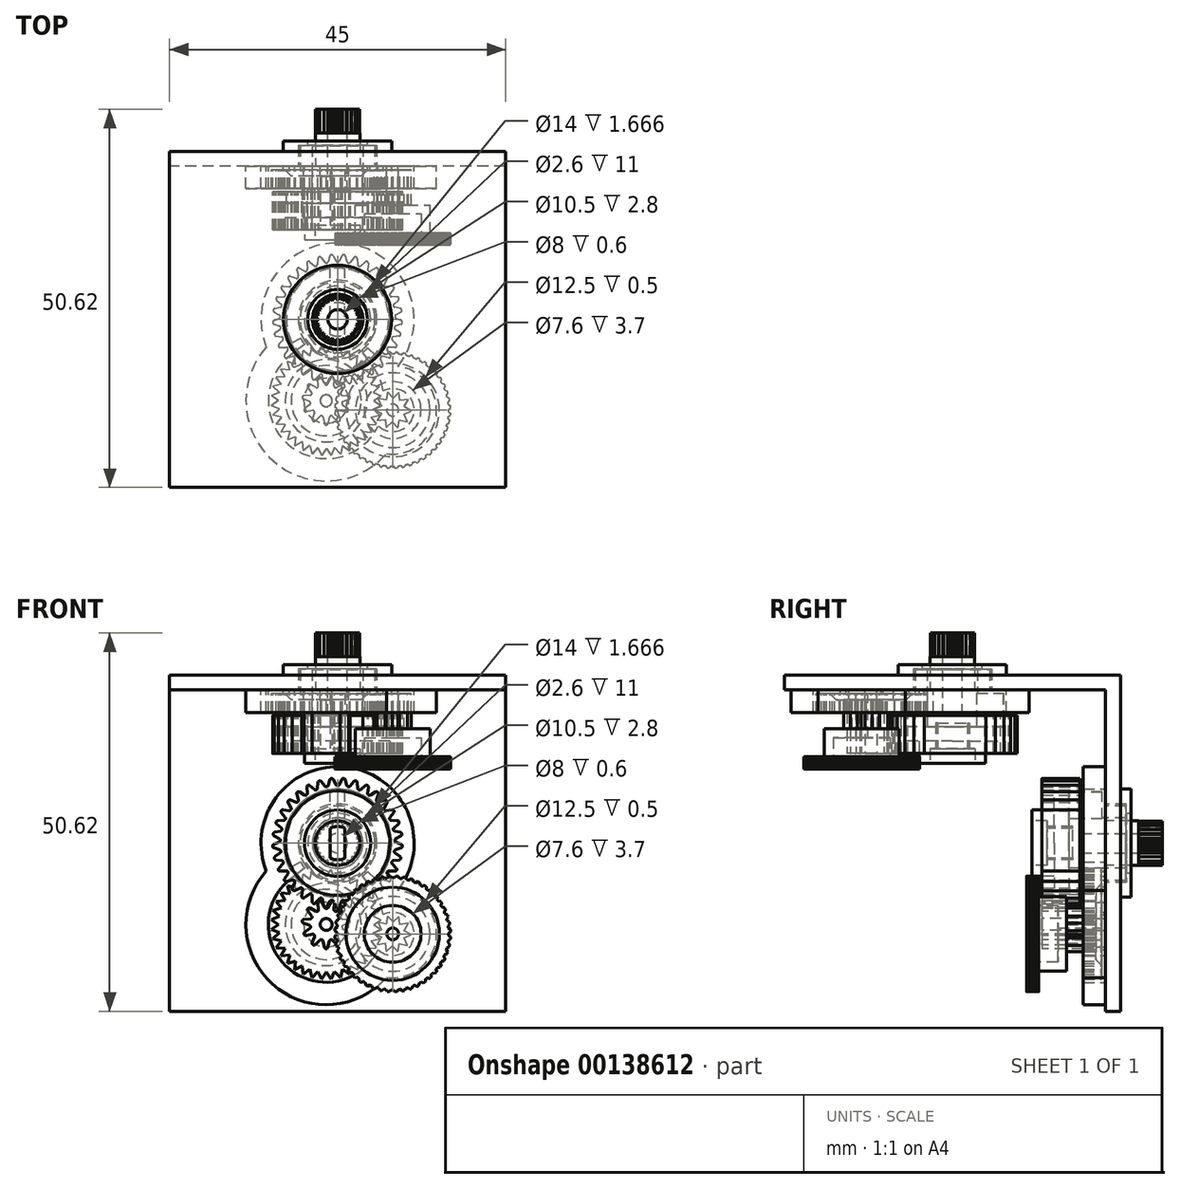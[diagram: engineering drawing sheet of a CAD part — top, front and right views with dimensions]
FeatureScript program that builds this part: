
annotation { "Feature Type Name" : "Feature", "Feature Type Description" : "" }
export const myFeature = defineFeature(function(context is Context, id is Id, definition is map)
    precondition{}
    {
        {
            var Q0;
            Q0=qCreatedBy(makeId("Front.planeOp"),FACE);
            var sketch = newSketch(context, id + "F0", { "sketchPlane" : qUnion([Q0])});
            skLineSegment(sketch, "E0", {"start": v(0, 0) * mm, "end": v(0, 17.46) * mm, "construction": true});
            skLineSegment(sketch, "E1", {"start": v(0, 0) * mm, "end": v(-4.45, 0) * mm});
            skLineSegment(sketch, "E2", {"start": v(-4.45, 0) * mm, "end": v(-4.45, 1.33) * mm});
            skLineSegment(sketch, "E3", {"start": v(-4.45, 1.33) * mm, "end": v(-8.7, 1.33) * mm});
            skLineSegment(sketch, "E4", {"start": v(-8.7, 1.33) * mm, "end": v(-8.7, 6.41) * mm});
            skLineSegment(sketch, "E5", {"start": v(-8.7, 6.41) * mm, "end": v(-3.38, 6.41) * mm});
            skLineSegment(sketch, "E6", {"start": v(-3.38, 6.41) * mm, "end": v(-3.38, 9.84) * mm});
            skLineSegment(sketch, "E7", {"start": v(-3.38, 9.84) * mm, "end": v(-2.98, 9.84) * mm});
            skLineSegment(sketch, "E8", {"start": v(-2.98, 9.84) * mm, "end": v(-2.98, 13.97) * mm});
            skLineSegment(sketch, "E9", {"start": v(-2.98, 13.97) * mm, "end": v(-2.98, 17.46) * mm});
            skLineSegment(sketch, "E10", {"start": v(-2.98, 17.46) * mm, "end": v(0, 17.46) * mm});
            skLineSegment(sketch, "E11", {"start": v(0, 0) * mm, "end": v(0, 17.46) * mm});
            skSolve(sketch);
        }
        {
            var Q0;
            Q0 = qSketchRegion(id + "F0", true);
            var Q1;
            Q1=sQuery(id+"F0.wireOp",EDGE,"E0");
            revolve(context, id + "F1", {"entities" : qUnion([Q0]), "axis" : qUnion([Q1]), "revolveType" : RevolveType.FULL});
        }
        {
            var Q0;
            Q0=makeQuery(id+"F1.opRevolve","SWEPT_FACE",FACE,{"disambiguationData":[OSD([sQuery(id+"F0.wireOp",EDGE,"E10")])]});
            var sketch = newSketch(context, id + "F2", { "sketchPlane" : qUnion([Q0])});
            skLineSegment(sketch, "E12", {"start": v(0, 0) * mm, "end": v(0, 2.98) * mm, "construction": true});
            skLineSegment(sketch, "E13", {"start": v(0, 0) * mm, "end": v(-0.39, 2.96) * mm, "construction": true});
            skLineSegment(sketch, "E14.MirrorCS", {"start": v(0, 0) * mm, "end": v(0.39, 2.96) * mm, "construction": true});
            skLineSegment(sketch, "E15", {"start": v(-0.39, 2.96) * mm, "end": v(0, 2.6) * mm});
            skLineSegment(sketch, "E16", {"start": v(0, 2.6) * mm, "end": v(0.39, 2.96) * mm});
            skLineSegment(sketch, "E17.1.0", {"start": v(-1.14, 2.76) * mm, "end": v(-0.67, 2.51) * mm});
            skLineSegment(sketch, "E17.1.1", {"start": v(-0.67, 2.51) * mm, "end": v(-0.39, 2.96) * mm});
            skLineSegment(sketch, "E17.2.0", {"start": v(-1.82, 2.37) * mm, "end": v(-1.3, 2.25) * mm});
            skLineSegment(sketch, "E17.2.1", {"start": v(-1.3, 2.25) * mm, "end": v(-1.14, 2.76) * mm});
            skLineSegment(sketch, "E17.3.0", {"start": v(-2.37, 1.82) * mm, "end": v(-1.84, 1.84) * mm});
            skLineSegment(sketch, "E17.3.1", {"start": v(-1.84, 1.84) * mm, "end": v(-1.82, 2.37) * mm});
            skLineSegment(sketch, "E17.4.0", {"start": v(-2.76, 1.14) * mm, "end": v(-2.25, 1.3) * mm});
            skLineSegment(sketch, "E17.4.1", {"start": v(-2.25, 1.3) * mm, "end": v(-2.37, 1.82) * mm});
            skLineSegment(sketch, "E17.5.0", {"start": v(-2.96, 0.39) * mm, "end": v(-2.51, 0.67) * mm});
            skLineSegment(sketch, "E17.5.1", {"start": v(-2.51, 0.67) * mm, "end": v(-2.76, 1.14) * mm});
            skLineSegment(sketch, "E17.6.0", {"start": v(-2.96, -0.39) * mm, "end": v(-2.6, 0) * mm});
            skLineSegment(sketch, "E17.6.1", {"start": v(-2.6, 0) * mm, "end": v(-2.96, 0.39) * mm});
            skLineSegment(sketch, "E17.7.0", {"start": v(-2.76, -1.14) * mm, "end": v(-2.51, -0.67) * mm});
            skLineSegment(sketch, "E17.7.1", {"start": v(-2.51, -0.67) * mm, "end": v(-2.96, -0.39) * mm});
            skLineSegment(sketch, "E17.8.0", {"start": v(-2.37, -1.82) * mm, "end": v(-2.25, -1.3) * mm});
            skLineSegment(sketch, "E17.8.1", {"start": v(-2.25, -1.3) * mm, "end": v(-2.76, -1.14) * mm});
            skLineSegment(sketch, "E17.9.0", {"start": v(-1.82, -2.37) * mm, "end": v(-1.84, -1.84) * mm});
            skLineSegment(sketch, "E17.9.1", {"start": v(-1.84, -1.84) * mm, "end": v(-2.37, -1.82) * mm});
            skLineSegment(sketch, "E17.10.0", {"start": v(-1.14, -2.76) * mm, "end": v(-1.3, -2.25) * mm});
            skLineSegment(sketch, "E17.10.1", {"start": v(-1.3, -2.25) * mm, "end": v(-1.82, -2.37) * mm});
            skLineSegment(sketch, "E17.11.0", {"start": v(-0.39, -2.96) * mm, "end": v(-0.67, -2.51) * mm});
            skLineSegment(sketch, "E17.11.1", {"start": v(-0.67, -2.51) * mm, "end": v(-1.14, -2.76) * mm});
            skLineSegment(sketch, "E17.12.0", {"start": v(0.39, -2.96) * mm, "end": v(0, -2.6) * mm});
            skLineSegment(sketch, "E17.12.1", {"start": v(0, -2.6) * mm, "end": v(-0.39, -2.96) * mm});
            skLineSegment(sketch, "E17.13.0", {"start": v(1.14, -2.76) * mm, "end": v(0.67, -2.51) * mm});
            skLineSegment(sketch, "E17.13.1", {"start": v(0.67, -2.51) * mm, "end": v(0.39, -2.96) * mm});
            skLineSegment(sketch, "E17.14.0", {"start": v(1.82, -2.37) * mm, "end": v(1.3, -2.25) * mm});
            skLineSegment(sketch, "E17.14.1", {"start": v(1.3, -2.25) * mm, "end": v(1.14, -2.76) * mm});
            skLineSegment(sketch, "E17.15.0", {"start": v(2.37, -1.82) * mm, "end": v(1.84, -1.84) * mm});
            skLineSegment(sketch, "E17.15.1", {"start": v(1.84, -1.84) * mm, "end": v(1.82, -2.37) * mm});
            skLineSegment(sketch, "E17.16.0", {"start": v(2.76, -1.14) * mm, "end": v(2.25, -1.3) * mm});
            skLineSegment(sketch, "E17.16.1", {"start": v(2.25, -1.3) * mm, "end": v(2.37, -1.82) * mm});
            skLineSegment(sketch, "E17.17.0", {"start": v(2.96, -0.39) * mm, "end": v(2.51, -0.67) * mm});
            skLineSegment(sketch, "E17.17.1", {"start": v(2.51, -0.67) * mm, "end": v(2.76, -1.14) * mm});
            skLineSegment(sketch, "E17.18.0", {"start": v(2.96, 0.39) * mm, "end": v(2.6, 0) * mm});
            skLineSegment(sketch, "E17.18.1", {"start": v(2.6, 0) * mm, "end": v(2.96, -0.39) * mm});
            skLineSegment(sketch, "E17.19.0", {"start": v(2.76, 1.14) * mm, "end": v(2.51, 0.67) * mm});
            skLineSegment(sketch, "E17.19.1", {"start": v(2.51, 0.67) * mm, "end": v(2.96, 0.39) * mm});
            skLineSegment(sketch, "E17.20.0", {"start": v(2.37, 1.82) * mm, "end": v(2.25, 1.3) * mm});
            skLineSegment(sketch, "E17.20.1", {"start": v(2.25, 1.3) * mm, "end": v(2.76, 1.14) * mm});
            skLineSegment(sketch, "E17.21.0", {"start": v(1.82, 2.37) * mm, "end": v(1.84, 1.84) * mm});
            skLineSegment(sketch, "E17.21.1", {"start": v(1.84, 1.84) * mm, "end": v(2.37, 1.82) * mm});
            skLineSegment(sketch, "E17.22.0", {"start": v(1.14, 2.76) * mm, "end": v(1.3, 2.25) * mm});
            skLineSegment(sketch, "E17.22.1", {"start": v(1.3, 2.25) * mm, "end": v(1.82, 2.37) * mm});
            skLineSegment(sketch, "E17.23.0", {"start": v(0.39, 2.96) * mm, "end": v(0.67, 2.51) * mm});
            skLineSegment(sketch, "E17.23.1", {"start": v(0.67, 2.51) * mm, "end": v(1.14, 2.76) * mm});
            skPoint(sketch, "E17.center", {"position": v(0, 0) * mm});
            skSolve(sketch);
        }
        {
            var Q0;
            {var subQ0=sQuery(id+"F2.wireOp",EDGE,"E17.2.0");Q0=makeQuery(id+"F2.imprint","IMPRINT",FACE,{"disambiguationData":[TD([[makeQuery(id+"F2.imprint","IMPRINT",EDGE,{"derivedFrom":subQ0}),1.0]])]});}
            var Q1;
            {var subQ0=sQuery(id+"F2.wireOp",EDGE,"E17.1.0");Q1=makeQuery(id+"F2.imprint","IMPRINT",FACE,{"disambiguationData":[TD([[makeQuery(id+"F2.imprint","IMPRINT",EDGE,{"derivedFrom":subQ0}),1.0]])]});}
            var Q2;
            {var subQ0=sQuery(id+"F2.wireOp",EDGE,"E15");Q2=makeQuery(id+"F2.imprint","IMPRINT",FACE,{"disambiguationData":[TD([[makeQuery(id+"F2.imprint","IMPRINT",EDGE,{"derivedFrom":subQ0}),1.0]])]});}
            var Q3;
            {var subQ0=sQuery(id+"F2.wireOp",EDGE,"E17.23.0");Q3=makeQuery(id+"F2.imprint","IMPRINT",FACE,{"disambiguationData":[TD([[makeQuery(id+"F2.imprint","IMPRINT",EDGE,{"derivedFrom":subQ0}),1.0]])]});}
            var Q4;
            {var subQ0=sQuery(id+"F2.wireOp",EDGE,"E17.22.0");Q4=makeQuery(id+"F2.imprint","IMPRINT",FACE,{"disambiguationData":[TD([[makeQuery(id+"F2.imprint","IMPRINT",EDGE,{"derivedFrom":subQ0}),1.0]])]});}
            var Q5;
            {var subQ0=sQuery(id+"F2.wireOp",EDGE,"E17.21.0");Q5=makeQuery(id+"F2.imprint","IMPRINT",FACE,{"disambiguationData":[TD([[makeQuery(id+"F2.imprint","IMPRINT",EDGE,{"derivedFrom":subQ0}),1.0]])]});}
            var Q6;
            {var subQ0=sQuery(id+"F2.wireOp",EDGE,"E17.20.0");Q6=makeQuery(id+"F2.imprint","IMPRINT",FACE,{"disambiguationData":[TD([[makeQuery(id+"F2.imprint","IMPRINT",EDGE,{"derivedFrom":subQ0}),1.0]])]});}
            var Q7;
            {var subQ0=sQuery(id+"F2.wireOp",EDGE,"E17.19.0");Q7=makeQuery(id+"F2.imprint","IMPRINT",FACE,{"disambiguationData":[TD([[makeQuery(id+"F2.imprint","IMPRINT",EDGE,{"derivedFrom":subQ0}),1.0]])]});}
            var Q8;
            {var subQ0=sQuery(id+"F2.wireOp",EDGE,"E17.18.0");Q8=makeQuery(id+"F2.imprint","IMPRINT",FACE,{"disambiguationData":[TD([[makeQuery(id+"F2.imprint","IMPRINT",EDGE,{"derivedFrom":subQ0}),1.0]])]});}
            var Q9;
            {var subQ0=sQuery(id+"F2.wireOp",EDGE,"E17.17.0");Q9=makeQuery(id+"F2.imprint","IMPRINT",FACE,{"disambiguationData":[TD([[makeQuery(id+"F2.imprint","IMPRINT",EDGE,{"derivedFrom":subQ0}),1.0]])]});}
            var Q10;
            {var subQ0=sQuery(id+"F2.wireOp",EDGE,"E17.16.0");Q10=makeQuery(id+"F2.imprint","IMPRINT",FACE,{"disambiguationData":[TD([[makeQuery(id+"F2.imprint","IMPRINT",EDGE,{"derivedFrom":subQ0}),1.0]])]});}
            var Q11;
            {var subQ0=sQuery(id+"F2.wireOp",EDGE,"E17.15.0");Q11=makeQuery(id+"F2.imprint","IMPRINT",FACE,{"disambiguationData":[TD([[makeQuery(id+"F2.imprint","IMPRINT",EDGE,{"derivedFrom":subQ0}),1.0]])]});}
            var Q12;
            {var subQ0=sQuery(id+"F2.wireOp",EDGE,"E17.14.0");Q12=makeQuery(id+"F2.imprint","IMPRINT",FACE,{"disambiguationData":[TD([[makeQuery(id+"F2.imprint","IMPRINT",EDGE,{"derivedFrom":subQ0}),1.0]])]});}
            var Q13;
            {var subQ0=sQuery(id+"F2.wireOp",EDGE,"E17.13.0");Q13=makeQuery(id+"F2.imprint","IMPRINT",FACE,{"disambiguationData":[TD([[makeQuery(id+"F2.imprint","IMPRINT",EDGE,{"derivedFrom":subQ0}),1.0]])]});}
            var Q14;
            {var subQ0=sQuery(id+"F2.wireOp",EDGE,"E17.12.0");Q14=makeQuery(id+"F2.imprint","IMPRINT",FACE,{"disambiguationData":[TD([[makeQuery(id+"F2.imprint","IMPRINT",EDGE,{"derivedFrom":subQ0}),1.0]])]});}
            var Q15;
            {var subQ0=sQuery(id+"F2.wireOp",EDGE,"E17.11.0");Q15=makeQuery(id+"F2.imprint","IMPRINT",FACE,{"disambiguationData":[TD([[makeQuery(id+"F2.imprint","IMPRINT",EDGE,{"derivedFrom":subQ0}),1.0]])]});}
            var Q16;
            {var subQ0=sQuery(id+"F2.wireOp",EDGE,"E17.10.0");Q16=makeQuery(id+"F2.imprint","IMPRINT",FACE,{"disambiguationData":[TD([[makeQuery(id+"F2.imprint","IMPRINT",EDGE,{"derivedFrom":subQ0}),1.0]])]});}
            var Q17;
            {var subQ0=sQuery(id+"F2.wireOp",EDGE,"E17.9.0");Q17=makeQuery(id+"F2.imprint","IMPRINT",FACE,{"disambiguationData":[TD([[makeQuery(id+"F2.imprint","IMPRINT",EDGE,{"derivedFrom":subQ0}),1.0]])]});}
            var Q18;
            {var subQ0=sQuery(id+"F2.wireOp",EDGE,"E17.8.0");Q18=makeQuery(id+"F2.imprint","IMPRINT",FACE,{"disambiguationData":[TD([[makeQuery(id+"F2.imprint","IMPRINT",EDGE,{"derivedFrom":subQ0}),1.0]])]});}
            var Q19;
            {var subQ0=sQuery(id+"F2.wireOp",EDGE,"E17.7.0");Q19=makeQuery(id+"F2.imprint","IMPRINT",FACE,{"disambiguationData":[TD([[makeQuery(id+"F2.imprint","IMPRINT",EDGE,{"derivedFrom":subQ0}),1.0]])]});}
            var Q20;
            {var subQ0=sQuery(id+"F2.wireOp",EDGE,"E17.6.0");Q20=makeQuery(id+"F2.imprint","IMPRINT",FACE,{"disambiguationData":[TD([[makeQuery(id+"F2.imprint","IMPRINT",EDGE,{"derivedFrom":subQ0}),1.0]])]});}
            var Q21;
            {var subQ0=sQuery(id+"F2.wireOp",EDGE,"E17.5.0");Q21=makeQuery(id+"F2.imprint","IMPRINT",FACE,{"disambiguationData":[TD([[makeQuery(id+"F2.imprint","IMPRINT",EDGE,{"derivedFrom":subQ0}),1.0]])]});}
            var Q22;
            {var subQ0=sQuery(id+"F2.wireOp",EDGE,"E17.4.0");Q22=makeQuery(id+"F2.imprint","IMPRINT",FACE,{"disambiguationData":[TD([[makeQuery(id+"F2.imprint","IMPRINT",EDGE,{"derivedFrom":subQ0}),1.0]])]});}
            var Q23;
            {var subQ0=sQuery(id+"F2.wireOp",EDGE,"E17.3.0");Q23=makeQuery(id+"F2.imprint","IMPRINT",FACE,{"disambiguationData":[TD([[makeQuery(id+"F2.imprint","IMPRINT",EDGE,{"derivedFrom":subQ0}),1.0]])]});}
            extrude(context, id + "F3", {"entities" : qUnion([Q0, Q1, Q2, Q3, Q4, Q5, Q6, Q7, Q8, Q9, Q10, Q11, Q12, Q13, Q14, Q15, Q16, Q17, Q18, Q19, Q20, Q21, Q22, Q23]), "operationType" : NewBodyOperationType.REMOVE, "oppositeDirection" : true, "depth" : 3.17 * mm});
        }
        {
            var Q0;
            Q0=makeQuery(id+"F1.opRevolve","SWEPT_FACE",FACE,{"disambiguationData":[OSD([sQuery(id+"F0.wireOp",EDGE,"E5")])]});
            var sketch = newSketch(context, id + "F4", { "sketchPlane" : qUnion([Q0])});
            skLineSegment(sketch, "E18", {"start": v(0, 0) * mm, "end": v(0, 8.7) * mm, "construction": true});
            skLineSegment(sketch, "E19", {"start": v(0, 0) * mm, "end": v(-0.83, 8.66) * mm, "construction": true});
            skLineSegment(sketch, "E20.MirrorCS", {"start": v(0, 0) * mm, "end": v(0.83, 8.66) * mm, "construction": true});
            skArc(sketch, "E21", {"start": v(-0.58, 8.52) * mm, "mid": v(-0.68, 8.63) * mm, "end": v(-0.83, 8.66) * mm});
            skArc(sketch, "E22", {"start": v(-0.23, 7.82) * mm, "mid": v(0, 7.68) * mm, "end": v(0.23, 7.82) * mm});
            skLineSegment(sketch, "E23", {"start": v(-0.58, 8.52) * mm, "end": v(-0.23, 7.82) * mm});
            skLineSegment(sketch, "E24.MirrorCS", {"start": v(0.58, 8.52) * mm, "end": v(0.23, 7.82) * mm});
            skArc(sketch, "E25.MirrorC", {"start": v(0.58, 8.52) * mm, "mid": v(0.68, 8.63) * mm, "end": v(0.83, 8.66) * mm});
            skCircle(sketch, "E26", {"center": v(0, 0) * mm, "radius": 8.7 * mm});
            skArc(sketch, "E27.1.0", {"start": v(-1.7, 7.64) * mm, "mid": v(-1.45, 7.54) * mm, "end": v(-1.26, 7.73) * mm});
            skLineSegment(sketch, "E27.1.1", {"start": v(-2.18, 8.26) * mm, "end": v(-1.7, 7.64) * mm});
            skLineSegment(sketch, "E27.1.2", {"start": v(-1.05, 8.48) * mm, "end": v(-1.26, 7.73) * mm});
            skArc(sketch, "E27.1.3", {"start": v(-2.18, 8.26) * mm, "mid": v(-2.3, 8.34) * mm, "end": v(-2.45, 8.35) * mm});
            skArc(sketch, "E27.1.4", {"start": v(-1.05, 8.48) * mm, "mid": v(-0.97, 8.6) * mm, "end": v(-0.83, 8.66) * mm});
            skArc(sketch, "E27.2.0", {"start": v(-3.12, 7.18) * mm, "mid": v(-2.86, 7.13) * mm, "end": v(-2.7, 7.35) * mm});
            skLineSegment(sketch, "E27.2.1", {"start": v(-3.7, 7.7) * mm, "end": v(-3.12, 7.18) * mm});
            skLineSegment(sketch, "E27.2.2", {"start": v(-2.63, 8.12) * mm, "end": v(-2.7, 7.35) * mm});
            skArc(sketch, "E27.2.3", {"start": v(-3.7, 7.7) * mm, "mid": v(-3.84, 7.76) * mm, "end": v(-3.99, 7.73) * mm});
            skArc(sketch, "E27.2.4", {"start": v(-2.63, 8.12) * mm, "mid": v(-2.58, 8.26) * mm, "end": v(-2.45, 8.35) * mm});
            skArc(sketch, "E27.3.0", {"start": v(-4.42, 6.46) * mm, "mid": v(-4.15, 6.46) * mm, "end": v(-4.04, 6.7) * mm});
            skLineSegment(sketch, "E27.3.1", {"start": v(-5.1, 6.86) * mm, "end": v(-4.42, 6.46) * mm});
            skLineSegment(sketch, "E27.3.2", {"start": v(-4.12, 7.48) * mm, "end": v(-4.04, 6.7) * mm});
            skArc(sketch, "E27.3.3", {"start": v(-5.1, 6.86) * mm, "mid": v(-5.24, 6.9) * mm, "end": v(-5.38, 6.84) * mm});
            skArc(sketch, "E27.3.4", {"start": v(-4.12, 7.48) * mm, "mid": v(-4.1, 7.63) * mm, "end": v(-3.99, 7.73) * mm});
            skArc(sketch, "E27.4.0", {"start": v(-5.56, 5.5) * mm, "mid": v(-5.3, 5.56) * mm, "end": v(-5.23, 5.82) * mm});
            skLineSegment(sketch, "E27.4.1", {"start": v(-6.3, 5.77) * mm, "end": v(-5.56, 5.5) * mm});
            skLineSegment(sketch, "E27.4.2", {"start": v(-5.46, 6.56) * mm, "end": v(-5.23, 5.82) * mm});
            skArc(sketch, "E27.4.3", {"start": v(-6.3, 5.77) * mm, "mid": v(-6.45, 5.78) * mm, "end": v(-6.57, 5.7) * mm});
            skArc(sketch, "E27.4.4", {"start": v(-5.46, 6.56) * mm, "mid": v(-5.46, 6.71) * mm, "end": v(-5.38, 6.84) * mm});
            skArc(sketch, "E27.5.0", {"start": v(-6.5, 4.35) * mm, "mid": v(-6.26, 4.46) * mm, "end": v(-6.24, 4.72) * mm});
            skLineSegment(sketch, "E27.5.1", {"start": v(-7.27, 4.47) * mm, "end": v(-6.5, 4.35) * mm});
            skLineSegment(sketch, "E27.5.2", {"start": v(-6.6, 5.41) * mm, "end": v(-6.24, 4.72) * mm});
            skArc(sketch, "E27.5.3", {"start": v(-7.27, 4.47) * mm, "mid": v(-7.42, 4.45) * mm, "end": v(-7.53, 4.35) * mm});
            skArc(sketch, "E27.5.4", {"start": v(-6.6, 5.41) * mm, "mid": v(-6.64, 5.56) * mm, "end": v(-6.57, 5.7) * mm});
            skArc(sketch, "E27.6.0", {"start": v(-7.21, 3.04) * mm, "mid": v(-6.99, 3.2) * mm, "end": v(-7.02, 3.46) * mm});
            skLineSegment(sketch, "E27.6.1", {"start": v(-7.99, 3.02) * mm, "end": v(-7.21, 3.04) * mm});
            skLineSegment(sketch, "E27.6.2", {"start": v(-7.51, 4.06) * mm, "end": v(-7.02, 3.46) * mm});
            skArc(sketch, "E27.6.3", {"start": v(-7.99, 3.02) * mm, "mid": v(-8.13, 2.97) * mm, "end": v(-8.22, 2.85) * mm});
            skArc(sketch, "E27.6.4", {"start": v(-7.51, 4.06) * mm, "mid": v(-7.57, 4.2) * mm, "end": v(-7.53, 4.35) * mm});
            skArc(sketch, "E27.7.0", {"start": v(-7.66, 1.62) * mm, "mid": v(-7.47, 1.81) * mm, "end": v(-7.55, 2.07) * mm});
            skLineSegment(sketch, "E27.7.1", {"start": v(-8.42, 1.45) * mm, "end": v(-7.66, 1.62) * mm});
            skLineSegment(sketch, "E27.7.2", {"start": v(-8.14, 2.57) * mm, "end": v(-7.55, 2.07) * mm});
            skArc(sketch, "E27.7.3", {"start": v(-8.42, 1.45) * mm, "mid": v(-8.55, 1.37) * mm, "end": v(-8.61, 1.24) * mm});
            skArc(sketch, "E27.7.4", {"start": v(-8.14, 2.57) * mm, "mid": v(-8.23, 2.7) * mm, "end": v(-8.22, 2.85) * mm});
            skArc(sketch, "E27.8.0", {"start": v(-7.83, 0.15) * mm, "mid": v(-7.67, 0.37) * mm, "end": v(-7.8, 0.6) * mm});
            skLineSegment(sketch, "E27.8.1", {"start": v(-8.54, -0.17) * mm, "end": v(-7.83, 0.15) * mm});
            skLineSegment(sketch, "E27.8.2", {"start": v(-8.48, 0.98) * mm, "end": v(-7.8, 0.6) * mm});
            skArc(sketch, "E27.8.3", {"start": v(-8.54, -0.17) * mm, "mid": v(-8.65, -0.27) * mm, "end": v(-8.69, -0.41) * mm});
            skArc(sketch, "E27.8.4", {"start": v(-8.48, 0.98) * mm, "mid": v(-8.59, 1.09) * mm, "end": v(-8.61, 1.24) * mm});
            skArc(sketch, "E27.9.0", {"start": v(-7.71, -1.34) * mm, "mid": v(-7.6, -1.1) * mm, "end": v(-7.78, -0.89) * mm});
            skLineSegment(sketch, "E27.9.1", {"start": v(-8.35, -1.78) * mm, "end": v(-7.71, -1.34) * mm});
            skLineSegment(sketch, "E27.9.2", {"start": v(-8.52, -0.64) * mm, "end": v(-7.78, -0.89) * mm});
            skArc(sketch, "E27.9.3", {"start": v(-8.35, -1.78) * mm, "mid": v(-8.44, -1.9) * mm, "end": v(-8.45, -2.05) * mm});
            skArc(sketch, "E27.9.4", {"start": v(-8.52, -0.64) * mm, "mid": v(-8.64, -0.56) * mm, "end": v(-8.69, -0.41) * mm});
            skArc(sketch, "E27.10.0", {"start": v(-7.32, -2.77) * mm, "mid": v(-7.26, -2.51) * mm, "end": v(-7.47, -2.34) * mm});
            skLineSegment(sketch, "E27.10.1", {"start": v(-7.86, -3.33) * mm, "end": v(-7.32, -2.77) * mm});
            skLineSegment(sketch, "E27.10.2", {"start": v(-8.24, -2.24) * mm, "end": v(-7.47, -2.34) * mm});
            skArc(sketch, "E27.10.3", {"start": v(-7.86, -3.33) * mm, "mid": v(-7.93, -3.46) * mm, "end": v(-7.91, -3.61) * mm});
            skArc(sketch, "E27.10.4", {"start": v(-8.24, -2.24) * mm, "mid": v(-8.38, -2.18) * mm, "end": v(-8.45, -2.05) * mm});
            skArc(sketch, "E27.11.0", {"start": v(-6.66, -4.1) * mm, "mid": v(-6.65, -3.84) * mm, "end": v(-6.89, -3.72) * mm});
            skLineSegment(sketch, "E27.11.1", {"start": v(-7.1, -4.76) * mm, "end": v(-6.66, -4.1) * mm});
            skLineSegment(sketch, "E27.11.2", {"start": v(-7.67, -3.76) * mm, "end": v(-6.89, -3.72) * mm});
            skArc(sketch, "E27.11.3", {"start": v(-7.1, -4.76) * mm, "mid": v(-7.13, -4.9) * mm, "end": v(-7.09, -5.05) * mm});
            skArc(sketch, "E27.11.4", {"start": v(-7.67, -3.76) * mm, "mid": v(-7.81, -3.73) * mm, "end": v(-7.91, -3.61) * mm});
            skArc(sketch, "E27.12.0", {"start": v(-5.76, -5.3) * mm, "mid": v(-5.8, -5.03) * mm, "end": v(-6.06, -4.95) * mm});
            skLineSegment(sketch, "E27.12.1", {"start": v(-6.06, -6.01) * mm, "end": v(-5.76, -5.3) * mm});
            skLineSegment(sketch, "E27.12.2", {"start": v(-6.82, -5.14) * mm, "end": v(-6.06, -4.95) * mm});
            skArc(sketch, "E27.12.3", {"start": v(-6.06, -6.01) * mm, "mid": v(-6.08, -6.16) * mm, "end": v(-6, -6.3) * mm});
            skArc(sketch, "E27.12.4", {"start": v(-6.82, -5.14) * mm, "mid": v(-6.97, -5.14) * mm, "end": v(-7.09, -5.05) * mm});
            skArc(sketch, "E27.13.0", {"start": v(-4.66, -6.3) * mm, "mid": v(-4.75, -6.04) * mm, "end": v(-5.02, -6) * mm});
            skLineSegment(sketch, "E27.13.1", {"start": v(-4.81, -7.05) * mm, "end": v(-4.66, -6.3) * mm});
            skLineSegment(sketch, "E27.13.2", {"start": v(-5.72, -6.34) * mm, "end": v(-5.02, -6) * mm});
            skArc(sketch, "E27.13.3", {"start": v(-4.81, -7.05) * mm, "mid": v(-4.8, -7.2) * mm, "end": v(-4.7, -7.32) * mm});
            skArc(sketch, "E27.13.4", {"start": v(-5.72, -6.34) * mm, "mid": v(-5.87, -6.36) * mm, "end": v(-6, -6.3) * mm});
            skArc(sketch, "E27.14.0", {"start": v(-3.38, -7.06) * mm, "mid": v(-3.52, -6.83) * mm, "end": v(-3.79, -6.85) * mm});
            skLineSegment(sketch, "E27.14.1", {"start": v(-3.4, -7.84) * mm, "end": v(-3.38, -7.06) * mm});
            skLineSegment(sketch, "E27.14.2", {"start": v(-4.42, -7.3) * mm, "end": v(-3.79, -6.85) * mm});
            skArc(sketch, "E27.14.3", {"start": v(-3.4, -7.84) * mm, "mid": v(-3.35, -7.98) * mm, "end": v(-3.23, -8.08) * mm});
            skArc(sketch, "E27.14.4", {"start": v(-4.42, -7.3) * mm, "mid": v(-4.56, -7.36) * mm, "end": v(-4.7, -7.32) * mm});
            skArc(sketch, "E27.15.0", {"start": v(-1.99, -7.57) * mm, "mid": v(-2.16, -7.37) * mm, "end": v(-2.42, -7.44) * mm});
            skLineSegment(sketch, "E27.15.1", {"start": v(-1.85, -8.34) * mm, "end": v(-1.99, -7.57) * mm});
            skLineSegment(sketch, "E27.15.2", {"start": v(-2.95, -8.01) * mm, "end": v(-2.42, -7.44) * mm});
            skArc(sketch, "E27.15.3", {"start": v(-1.85, -8.34) * mm, "mid": v(-1.78, -8.47) * mm, "end": v(-1.65, -8.54) * mm});
            skArc(sketch, "E27.15.4", {"start": v(-2.95, -8.01) * mm, "mid": v(-3.08, -8.09) * mm, "end": v(-3.23, -8.08) * mm});
            skArc(sketch, "E27.16.0", {"start": v(-0.52, -7.81) * mm, "mid": v(-0.73, -7.65) * mm, "end": v(-0.97, -7.77) * mm});
            skLineSegment(sketch, "E27.16.1", {"start": v(-0.24, -8.54) * mm, "end": v(-0.52, -7.81) * mm});
            skLineSegment(sketch, "E27.16.2", {"start": v(-1.38, -8.43) * mm, "end": v(-0.97, -7.77) * mm});
            skArc(sketch, "E27.16.3", {"start": v(-0.24, -8.54) * mm, "mid": v(-0.14, -8.65) * mm, "end": v(0, -8.7) * mm});
            skArc(sketch, "E27.16.4", {"start": v(-1.38, -8.43) * mm, "mid": v(-1.5, -8.53) * mm, "end": v(-1.65, -8.54) * mm});
            skArc(sketch, "E27.17.0", {"start": v(0.97, -7.77) * mm, "mid": v(0.73, -7.65) * mm, "end": v(0.52, -7.81) * mm});
            skLineSegment(sketch, "E27.17.1", {"start": v(1.38, -8.43) * mm, "end": v(0.97, -7.77) * mm});
            skLineSegment(sketch, "E27.17.2", {"start": v(0.24, -8.54) * mm, "end": v(0.52, -7.81) * mm});
            skArc(sketch, "E27.17.3", {"start": v(1.38, -8.43) * mm, "mid": v(1.5, -8.53) * mm, "end": v(1.65, -8.54) * mm});
            skArc(sketch, "E27.17.4", {"start": v(0.24, -8.54) * mm, "mid": v(0.14, -8.65) * mm, "end": v(0, -8.7) * mm});
            skArc(sketch, "E27.18.0", {"start": v(2.42, -7.44) * mm, "mid": v(2.16, -7.37) * mm, "end": v(1.99, -7.57) * mm});
            skLineSegment(sketch, "E27.18.1", {"start": v(2.95, -8.01) * mm, "end": v(2.42, -7.44) * mm});
            skLineSegment(sketch, "E27.18.2", {"start": v(1.85, -8.34) * mm, "end": v(1.99, -7.57) * mm});
            skArc(sketch, "E27.18.3", {"start": v(2.95, -8.01) * mm, "mid": v(3.08, -8.09) * mm, "end": v(3.23, -8.08) * mm});
            skArc(sketch, "E27.18.4", {"start": v(1.85, -8.34) * mm, "mid": v(1.78, -8.47) * mm, "end": v(1.65, -8.54) * mm});
            skArc(sketch, "E27.19.0", {"start": v(3.79, -6.85) * mm, "mid": v(3.52, -6.83) * mm, "end": v(3.38, -7.06) * mm});
            skLineSegment(sketch, "E27.19.1", {"start": v(4.42, -7.3) * mm, "end": v(3.79, -6.85) * mm});
            skLineSegment(sketch, "E27.19.2", {"start": v(3.4, -7.84) * mm, "end": v(3.38, -7.06) * mm});
            skArc(sketch, "E27.19.3", {"start": v(4.42, -7.3) * mm, "mid": v(4.56, -7.36) * mm, "end": v(4.7, -7.32) * mm});
            skArc(sketch, "E27.19.4", {"start": v(3.4, -7.84) * mm, "mid": v(3.35, -7.98) * mm, "end": v(3.23, -8.08) * mm});
            skArc(sketch, "E27.20.0", {"start": v(5.02, -6) * mm, "mid": v(4.75, -6.04) * mm, "end": v(4.66, -6.3) * mm});
            skLineSegment(sketch, "E27.20.1", {"start": v(5.72, -6.34) * mm, "end": v(5.02, -6) * mm});
            skLineSegment(sketch, "E27.20.2", {"start": v(4.81, -7.05) * mm, "end": v(4.66, -6.3) * mm});
            skArc(sketch, "E27.20.3", {"start": v(5.72, -6.34) * mm, "mid": v(5.87, -6.36) * mm, "end": v(6, -6.3) * mm});
            skArc(sketch, "E27.20.4", {"start": v(4.81, -7.05) * mm, "mid": v(4.8, -7.2) * mm, "end": v(4.7, -7.32) * mm});
            skArc(sketch, "E27.21.0", {"start": v(6.06, -4.95) * mm, "mid": v(5.8, -5.03) * mm, "end": v(5.76, -5.3) * mm});
            skLineSegment(sketch, "E27.21.1", {"start": v(6.82, -5.14) * mm, "end": v(6.06, -4.95) * mm});
            skLineSegment(sketch, "E27.21.2", {"start": v(6.06, -6.01) * mm, "end": v(5.76, -5.3) * mm});
            skArc(sketch, "E27.21.3", {"start": v(6.82, -5.14) * mm, "mid": v(6.97, -5.14) * mm, "end": v(7.09, -5.05) * mm});
            skArc(sketch, "E27.21.4", {"start": v(6.06, -6.01) * mm, "mid": v(6.08, -6.16) * mm, "end": v(6, -6.3) * mm});
            skArc(sketch, "E27.22.0", {"start": v(6.89, -3.72) * mm, "mid": v(6.65, -3.84) * mm, "end": v(6.66, -4.1) * mm});
            skLineSegment(sketch, "E27.22.1", {"start": v(7.67, -3.76) * mm, "end": v(6.89, -3.72) * mm});
            skLineSegment(sketch, "E27.22.2", {"start": v(7.1, -4.76) * mm, "end": v(6.66, -4.1) * mm});
            skArc(sketch, "E27.22.3", {"start": v(7.67, -3.76) * mm, "mid": v(7.81, -3.73) * mm, "end": v(7.91, -3.61) * mm});
            skArc(sketch, "E27.22.4", {"start": v(7.1, -4.76) * mm, "mid": v(7.13, -4.9) * mm, "end": v(7.09, -5.05) * mm});
            skArc(sketch, "E27.23.0", {"start": v(7.47, -2.34) * mm, "mid": v(7.26, -2.51) * mm, "end": v(7.32, -2.77) * mm});
            skLineSegment(sketch, "E27.23.1", {"start": v(8.24, -2.24) * mm, "end": v(7.47, -2.34) * mm});
            skLineSegment(sketch, "E27.23.2", {"start": v(7.86, -3.33) * mm, "end": v(7.32, -2.77) * mm});
            skArc(sketch, "E27.23.3", {"start": v(8.24, -2.24) * mm, "mid": v(8.38, -2.18) * mm, "end": v(8.45, -2.05) * mm});
            skArc(sketch, "E27.23.4", {"start": v(7.86, -3.33) * mm, "mid": v(7.93, -3.46) * mm, "end": v(7.91, -3.61) * mm});
            skArc(sketch, "E27.24.0", {"start": v(7.78, -0.89) * mm, "mid": v(7.6, -1.1) * mm, "end": v(7.71, -1.34) * mm});
            skLineSegment(sketch, "E27.24.1", {"start": v(8.52, -0.64) * mm, "end": v(7.78, -0.89) * mm});
            skLineSegment(sketch, "E27.24.2", {"start": v(8.35, -1.78) * mm, "end": v(7.71, -1.34) * mm});
            skArc(sketch, "E27.24.3", {"start": v(8.52, -0.64) * mm, "mid": v(8.64, -0.56) * mm, "end": v(8.69, -0.41) * mm});
            skArc(sketch, "E27.24.4", {"start": v(8.35, -1.78) * mm, "mid": v(8.44, -1.9) * mm, "end": v(8.45, -2.05) * mm});
            skArc(sketch, "E27.25.0", {"start": v(7.8, 0.6) * mm, "mid": v(7.67, 0.37) * mm, "end": v(7.83, 0.15) * mm});
            skLineSegment(sketch, "E27.25.1", {"start": v(8.48, 0.98) * mm, "end": v(7.8, 0.6) * mm});
            skLineSegment(sketch, "E27.25.2", {"start": v(8.54, -0.17) * mm, "end": v(7.83, 0.15) * mm});
            skArc(sketch, "E27.25.3", {"start": v(8.48, 0.98) * mm, "mid": v(8.59, 1.09) * mm, "end": v(8.61, 1.24) * mm});
            skArc(sketch, "E27.25.4", {"start": v(8.54, -0.17) * mm, "mid": v(8.65, -0.27) * mm, "end": v(8.69, -0.41) * mm});
            skArc(sketch, "E27.26.0", {"start": v(7.55, 2.07) * mm, "mid": v(7.47, 1.81) * mm, "end": v(7.66, 1.62) * mm});
            skLineSegment(sketch, "E27.26.1", {"start": v(8.14, 2.57) * mm, "end": v(7.55, 2.07) * mm});
            skLineSegment(sketch, "E27.26.2", {"start": v(8.42, 1.45) * mm, "end": v(7.66, 1.62) * mm});
            skArc(sketch, "E27.26.3", {"start": v(8.14, 2.57) * mm, "mid": v(8.23, 2.7) * mm, "end": v(8.22, 2.85) * mm});
            skArc(sketch, "E27.26.4", {"start": v(8.42, 1.45) * mm, "mid": v(8.55, 1.37) * mm, "end": v(8.61, 1.24) * mm});
            skArc(sketch, "E27.27.0", {"start": v(7.02, 3.46) * mm, "mid": v(6.99, 3.2) * mm, "end": v(7.21, 3.04) * mm});
            skLineSegment(sketch, "E27.27.1", {"start": v(7.51, 4.06) * mm, "end": v(7.02, 3.46) * mm});
            skLineSegment(sketch, "E27.27.2", {"start": v(7.99, 3.02) * mm, "end": v(7.21, 3.04) * mm});
            skArc(sketch, "E27.27.3", {"start": v(7.51, 4.06) * mm, "mid": v(7.57, 4.2) * mm, "end": v(7.53, 4.35) * mm});
            skArc(sketch, "E27.27.4", {"start": v(7.99, 3.02) * mm, "mid": v(8.13, 2.97) * mm, "end": v(8.22, 2.85) * mm});
            skArc(sketch, "E27.28.0", {"start": v(6.24, 4.72) * mm, "mid": v(6.26, 4.46) * mm, "end": v(6.5, 4.35) * mm});
            skLineSegment(sketch, "E27.28.1", {"start": v(6.6, 5.41) * mm, "end": v(6.24, 4.72) * mm});
            skLineSegment(sketch, "E27.28.2", {"start": v(7.27, 4.47) * mm, "end": v(6.5, 4.35) * mm});
            skArc(sketch, "E27.28.3", {"start": v(6.6, 5.41) * mm, "mid": v(6.64, 5.56) * mm, "end": v(6.57, 5.7) * mm});
            skArc(sketch, "E27.28.4", {"start": v(7.27, 4.47) * mm, "mid": v(7.42, 4.45) * mm, "end": v(7.53, 4.35) * mm});
            skArc(sketch, "E27.29.0", {"start": v(5.23, 5.82) * mm, "mid": v(5.3, 5.56) * mm, "end": v(5.56, 5.5) * mm});
            skLineSegment(sketch, "E27.29.1", {"start": v(5.46, 6.56) * mm, "end": v(5.23, 5.82) * mm});
            skLineSegment(sketch, "E27.29.2", {"start": v(6.3, 5.77) * mm, "end": v(5.56, 5.5) * mm});
            skArc(sketch, "E27.29.3", {"start": v(5.46, 6.56) * mm, "mid": v(5.46, 6.71) * mm, "end": v(5.38, 6.84) * mm});
            skArc(sketch, "E27.29.4", {"start": v(6.3, 5.77) * mm, "mid": v(6.45, 5.78) * mm, "end": v(6.57, 5.7) * mm});
            skArc(sketch, "E27.30.0", {"start": v(4.04, 6.7) * mm, "mid": v(4.15, 6.46) * mm, "end": v(4.42, 6.46) * mm});
            skLineSegment(sketch, "E27.30.1", {"start": v(4.12, 7.48) * mm, "end": v(4.04, 6.7) * mm});
            skLineSegment(sketch, "E27.30.2", {"start": v(5.1, 6.86) * mm, "end": v(4.42, 6.46) * mm});
            skArc(sketch, "E27.30.3", {"start": v(4.12, 7.48) * mm, "mid": v(4.1, 7.63) * mm, "end": v(3.99, 7.73) * mm});
            skArc(sketch, "E27.30.4", {"start": v(5.1, 6.86) * mm, "mid": v(5.24, 6.9) * mm, "end": v(5.38, 6.84) * mm});
            skArc(sketch, "E27.31.0", {"start": v(2.7, 7.35) * mm, "mid": v(2.86, 7.13) * mm, "end": v(3.12, 7.18) * mm});
            skLineSegment(sketch, "E27.31.1", {"start": v(2.63, 8.12) * mm, "end": v(2.7, 7.35) * mm});
            skLineSegment(sketch, "E27.31.2", {"start": v(3.7, 7.7) * mm, "end": v(3.12, 7.18) * mm});
            skArc(sketch, "E27.31.3", {"start": v(2.63, 8.12) * mm, "mid": v(2.58, 8.26) * mm, "end": v(2.45, 8.35) * mm});
            skArc(sketch, "E27.31.4", {"start": v(3.7, 7.7) * mm, "mid": v(3.84, 7.76) * mm, "end": v(3.99, 7.73) * mm});
            skArc(sketch, "E27.32.0", {"start": v(1.26, 7.73) * mm, "mid": v(1.45, 7.54) * mm, "end": v(1.7, 7.64) * mm});
            skLineSegment(sketch, "E27.32.1", {"start": v(1.05, 8.48) * mm, "end": v(1.26, 7.73) * mm});
            skLineSegment(sketch, "E27.32.2", {"start": v(2.18, 8.26) * mm, "end": v(1.7, 7.64) * mm});
            skArc(sketch, "E27.32.3", {"start": v(1.05, 8.48) * mm, "mid": v(0.97, 8.6) * mm, "end": v(0.83, 8.66) * mm});
            skArc(sketch, "E27.32.4", {"start": v(2.18, 8.26) * mm, "mid": v(2.3, 8.34) * mm, "end": v(2.45, 8.35) * mm});
            skSolve(sketch);
        }
        {
            var Q0;
            Q0=makeQuery(id+"F4.imprint","IMPRINT",FACE,{"disambiguationData":[TD([[makeQuery(id+"F4.imprint","IMPRINT",EDGE,{"derivedFrom":sQuery(id+"F4.wireOp",EDGE,"E27.3.0")}),1.0]])]});
            var Q1;
            Q1=makeQuery(id+"F4.imprint","IMPRINT",FACE,{"disambiguationData":[TD([[makeQuery(id+"F4.imprint","IMPRINT",EDGE,{"derivedFrom":sQuery(id+"F4.wireOp",EDGE,"E27.2.0")}),1.0]])]});
            var Q2;
            Q2=makeQuery(id+"F4.imprint","IMPRINT",FACE,{"disambiguationData":[TD([[makeQuery(id+"F4.imprint","IMPRINT",EDGE,{"derivedFrom":sQuery(id+"F4.wireOp",EDGE,"E27.1.0")}),1.0]])]});
            var Q3;
            {var subQ1=sQuery(id+"F4.wireOp",EDGE,"E21");Q3=makeQuery(id+"F4.imprint","IMPRINT",FACE,{"disambiguationData":[TD([[makeQuery(id+"F4.imprint","IMPRINT",EDGE,{"derivedFrom":subQ1}),-1.0]])]});}
            var Q4;
            Q4=makeQuery(id+"F4.imprint","IMPRINT",FACE,{"disambiguationData":[TD([[makeQuery(id+"F4.imprint","IMPRINT",EDGE,{"derivedFrom":sQuery(id+"F4.wireOp",EDGE,"E27.32.0")}),1.0]])]});
            var Q5;
            Q5=makeQuery(id+"F4.imprint","IMPRINT",FACE,{"disambiguationData":[TD([[makeQuery(id+"F4.imprint","IMPRINT",EDGE,{"derivedFrom":sQuery(id+"F4.wireOp",EDGE,"E27.31.0")}),1.0]])]});
            var Q6;
            Q6=makeQuery(id+"F4.imprint","IMPRINT",FACE,{"disambiguationData":[TD([[makeQuery(id+"F4.imprint","IMPRINT",EDGE,{"derivedFrom":sQuery(id+"F4.wireOp",EDGE,"E27.30.0")}),1.0]])]});
            var Q7;
            Q7=makeQuery(id+"F4.imprint","IMPRINT",FACE,{"disambiguationData":[TD([[makeQuery(id+"F4.imprint","IMPRINT",EDGE,{"derivedFrom":sQuery(id+"F4.wireOp",EDGE,"E27.29.0")}),1.0]])]});
            var Q8;
            Q8=makeQuery(id+"F4.imprint","IMPRINT",FACE,{"disambiguationData":[TD([[makeQuery(id+"F4.imprint","IMPRINT",EDGE,{"derivedFrom":sQuery(id+"F4.wireOp",EDGE,"E27.28.0")}),1.0]])]});
            var Q9;
            Q9=makeQuery(id+"F4.imprint","IMPRINT",FACE,{"disambiguationData":[TD([[makeQuery(id+"F4.imprint","IMPRINT",EDGE,{"derivedFrom":sQuery(id+"F4.wireOp",EDGE,"E27.27.0")}),1.0]])]});
            var Q10;
            Q10=makeQuery(id+"F4.imprint","IMPRINT",FACE,{"disambiguationData":[TD([[makeQuery(id+"F4.imprint","IMPRINT",EDGE,{"derivedFrom":sQuery(id+"F4.wireOp",EDGE,"E27.26.0")}),1.0]])]});
            var Q11;
            Q11=makeQuery(id+"F4.imprint","IMPRINT",FACE,{"disambiguationData":[TD([[makeQuery(id+"F4.imprint","IMPRINT",EDGE,{"derivedFrom":sQuery(id+"F4.wireOp",EDGE,"E27.25.0")}),1.0]])]});
            var Q12;
            Q12=makeQuery(id+"F4.imprint","IMPRINT",FACE,{"disambiguationData":[TD([[makeQuery(id+"F4.imprint","IMPRINT",EDGE,{"derivedFrom":sQuery(id+"F4.wireOp",EDGE,"E27.24.0")}),1.0]])]});
            var Q13;
            Q13=makeQuery(id+"F4.imprint","IMPRINT",FACE,{"disambiguationData":[TD([[makeQuery(id+"F4.imprint","IMPRINT",EDGE,{"derivedFrom":sQuery(id+"F4.wireOp",EDGE,"E27.23.0")}),1.0]])]});
            var Q14;
            Q14=makeQuery(id+"F4.imprint","IMPRINT",FACE,{"disambiguationData":[TD([[makeQuery(id+"F4.imprint","IMPRINT",EDGE,{"derivedFrom":sQuery(id+"F4.wireOp",EDGE,"E27.22.0")}),1.0]])]});
            var Q15;
            Q15=makeQuery(id+"F4.imprint","IMPRINT",FACE,{"disambiguationData":[TD([[makeQuery(id+"F4.imprint","IMPRINT",EDGE,{"derivedFrom":sQuery(id+"F4.wireOp",EDGE,"E27.21.0")}),1.0]])]});
            var Q16;
            Q16=makeQuery(id+"F4.imprint","IMPRINT",FACE,{"disambiguationData":[TD([[makeQuery(id+"F4.imprint","IMPRINT",EDGE,{"derivedFrom":sQuery(id+"F4.wireOp",EDGE,"E27.20.0")}),1.0]])]});
            var Q17;
            Q17=makeQuery(id+"F4.imprint","IMPRINT",FACE,{"disambiguationData":[TD([[makeQuery(id+"F4.imprint","IMPRINT",EDGE,{"derivedFrom":sQuery(id+"F4.wireOp",EDGE,"E27.19.0")}),1.0]])]});
            var Q18;
            Q18=makeQuery(id+"F4.imprint","IMPRINT",FACE,{"disambiguationData":[TD([[makeQuery(id+"F4.imprint","IMPRINT",EDGE,{"derivedFrom":sQuery(id+"F4.wireOp",EDGE,"E27.18.0")}),1.0]])]});
            var Q19;
            Q19=makeQuery(id+"F4.imprint","IMPRINT",FACE,{"disambiguationData":[TD([[makeQuery(id+"F4.imprint","IMPRINT",EDGE,{"derivedFrom":sQuery(id+"F4.wireOp",EDGE,"E27.17.0")}),1.0]])]});
            var Q20;
            Q20=makeQuery(id+"F4.imprint","IMPRINT",FACE,{"disambiguationData":[TD([[makeQuery(id+"F4.imprint","IMPRINT",EDGE,{"derivedFrom":sQuery(id+"F4.wireOp",EDGE,"E27.16.0")}),1.0]])]});
            var Q21;
            Q21=makeQuery(id+"F4.imprint","IMPRINT",FACE,{"disambiguationData":[TD([[makeQuery(id+"F4.imprint","IMPRINT",EDGE,{"derivedFrom":sQuery(id+"F4.wireOp",EDGE,"E27.14.0")}),1.0]])]});
            var Q22;
            Q22=makeQuery(id+"F4.imprint","IMPRINT",FACE,{"disambiguationData":[TD([[makeQuery(id+"F4.imprint","IMPRINT",EDGE,{"derivedFrom":sQuery(id+"F4.wireOp",EDGE,"E27.15.0")}),1.0]])]});
            var Q23;
            Q23=makeQuery(id+"F4.imprint","IMPRINT",FACE,{"disambiguationData":[TD([[makeQuery(id+"F4.imprint","IMPRINT",EDGE,{"derivedFrom":sQuery(id+"F4.wireOp",EDGE,"E27.13.0")}),1.0]])]});
            var Q24;
            Q24=makeQuery(id+"F4.imprint","IMPRINT",FACE,{"disambiguationData":[TD([[makeQuery(id+"F4.imprint","IMPRINT",EDGE,{"derivedFrom":sQuery(id+"F4.wireOp",EDGE,"E27.12.0")}),1.0]])]});
            var Q25;
            Q25=makeQuery(id+"F4.imprint","IMPRINT",FACE,{"disambiguationData":[TD([[makeQuery(id+"F4.imprint","IMPRINT",EDGE,{"derivedFrom":sQuery(id+"F4.wireOp",EDGE,"E27.11.0")}),1.0]])]});
            var Q26;
            Q26=makeQuery(id+"F4.imprint","IMPRINT",FACE,{"disambiguationData":[TD([[makeQuery(id+"F4.imprint","IMPRINT",EDGE,{"derivedFrom":sQuery(id+"F4.wireOp",EDGE,"E27.10.0")}),1.0]])]});
            var Q27;
            Q27=makeQuery(id+"F4.imprint","IMPRINT",FACE,{"disambiguationData":[TD([[makeQuery(id+"F4.imprint","IMPRINT",EDGE,{"derivedFrom":sQuery(id+"F4.wireOp",EDGE,"E27.9.0")}),1.0]])]});
            var Q28;
            Q28=makeQuery(id+"F4.imprint","IMPRINT",FACE,{"disambiguationData":[TD([[makeQuery(id+"F4.imprint","IMPRINT",EDGE,{"derivedFrom":sQuery(id+"F4.wireOp",EDGE,"E27.8.0")}),1.0]])]});
            var Q29;
            Q29=makeQuery(id+"F4.imprint","IMPRINT",FACE,{"disambiguationData":[TD([[makeQuery(id+"F4.imprint","IMPRINT",EDGE,{"derivedFrom":sQuery(id+"F4.wireOp",EDGE,"E27.7.0")}),1.0]])]});
            var Q30;
            Q30=makeQuery(id+"F4.imprint","IMPRINT",FACE,{"disambiguationData":[TD([[makeQuery(id+"F4.imprint","IMPRINT",EDGE,{"derivedFrom":sQuery(id+"F4.wireOp",EDGE,"E27.6.0")}),1.0]])]});
            var Q31;
            Q31=makeQuery(id+"F4.imprint","IMPRINT",FACE,{"disambiguationData":[TD([[makeQuery(id+"F4.imprint","IMPRINT",EDGE,{"derivedFrom":sQuery(id+"F4.wireOp",EDGE,"E27.5.0")}),1.0]])]});
            var Q32;
            Q32=makeQuery(id+"F4.imprint","IMPRINT",FACE,{"disambiguationData":[TD([[makeQuery(id+"F4.imprint","IMPRINT",EDGE,{"derivedFrom":sQuery(id+"F4.wireOp",EDGE,"E27.4.0")}),1.0]])]});
            extrude(context, id + "F5", {"entities" : qUnion([Q0, Q1, Q2, Q3, Q4, Q5, Q6, Q7, Q8, Q9, Q10, Q11, Q12, Q13, Q14, Q15, Q16, Q17, Q18, Q19, Q20, Q21, Q22, Q23, Q24, Q25, Q26, Q27, Q28, Q29, Q30, Q31, Q32]), "operationType" : NewBodyOperationType.REMOVE, "endBound" : BoundingType.THROUGH_ALL, "oppositeDirection" : true, "depth" : 5.08 * mm});
        }
        {
            var Q0;
            Q0=qCreatedBy(makeId("Top.planeOp"),FACE);
            var sketch = newSketch(context, id + "F6", { "sketchPlane" : qUnion([Q0])});
            skCircle(sketch, "E28", {"center": v(0, 0) * mm, "radius": 7 * mm});
            skCircle(sketch, "E29.0", {"center": v(0, 0) * mm, "radius": 4.45 * mm});
            skSolve(sketch);
        }
        {
            var Q0;
            Q0=makeQuery(id+"F6.imprint","IMPRINT",FACE,{"disambiguationData":[TD([[makeQuery(id+"F6.imprint","IMPRINT",EDGE,{"derivedFrom":sQuery(id+"F6.wireOp",EDGE,"E28")}),1.0]])]});
            extrude(context, id + "F7", {"entities" : qUnion([Q0]), "operationType" : NewBodyOperationType.REMOVE, "depth" : 3 * mm});
        }
        {
            var Q0;
            Q0=makeQuery(id+"F1.opRevolve","SWEPT_FACE",FACE,{"disambiguationData":[OSD([sQuery(id+"F0.wireOp",EDGE,"E1")])]});
            var sketch = newSketch(context, id + "F8", { "sketchPlane" : qUnion([Q0])});
            skCircle(sketch, "E30", {"center": v(0, 0) * mm, "radius": 3 * mm});
            skSolve(sketch);
        }
        {
            var Q0;
            Q0 = qSketchRegion(id + "F8", true);
            extrude(context, id + "F9", {"entities" : qUnion([Q0]), "operationType" : NewBodyOperationType.REMOVE, "oppositeDirection" : true, "depth" : 2 * mm});
        }
        {
            var Q0;
            Q0=makeQuery(id+"F1.opRevolve","SWEPT_FACE",FACE,{"disambiguationData":[OSD([sQuery(id+"F0.wireOp",EDGE,"E1")])]});
            var sketch = newSketch(context, id + "F10", { "sketchPlane" : qUnion([Q0])});
            skLineSegment(sketch, "E31.left", {"start": v(1, 2) * mm, "end": v(1, -2) * mm});
            skLineSegment(sketch, "E31.right", {"start": v(-1, 2) * mm, "end": v(-1, -2) * mm});
            skPoint(sketch, "E31.middle", {"position": v(0, 0) * mm});
            skArc(sketch, "E32", {"start": v(-1, -2) * mm, "mid": v(0, -2.24) * mm, "end": v(1, -2) * mm});
            skArc(sketch, "E33.trimOffspring", {"start": v(1, 2) * mm, "mid": v(0, 2.24) * mm, "end": v(-1, 2) * mm});
            skSolve(sketch);
        }
        {
            var Q0;
            Q0=makeQuery(id+"F10.imprint","IMPRINT",FACE,{"disambiguationData":[TD([[makeQuery(id+"F10.imprint","IMPRINT",EDGE,{"derivedFrom":sQuery(id+"F10.wireOp",EDGE,"E31.left")}),-1.0]])]});
            extrude(context, id + "F11", {"entities" : qUnion([Q0]), "operationType" : NewBodyOperationType.REMOVE, "oppositeDirection" : true, "depth" : 5.45 * mm});
        }
        {
            var Q0;
            Q0=makeQuery(id+"F1.opRevolve","SWEPT_FACE",FACE,{"disambiguationData":[OSD([sQuery(id+"F0.wireOp",EDGE,"E5")])]});
            var sketch = newSketch(context, id + "F12", { "sketchPlane" : qUnion([Q0])});
            skCircle(sketch, "E34", {"center": v(0, 0) * mm, "radius": 6.86 * mm});
            skCircle(sketch, "E35.0", {"center": v(0, 0) * mm, "radius": 3.38 * mm});
            skSolve(sketch);
        }
        {
            var Q0;
            Q0=makeQuery(id+"F12.imprint","IMPRINT",FACE,{"disambiguationData":[TD([[makeQuery(id+"F12.imprint","IMPRINT",EDGE,{"derivedFrom":sQuery(id+"F12.wireOp",EDGE,"E34")}),1.0]])]});
            extrude(context, id + "F13", {"entities" : qUnion([Q0]), "operationType" : NewBodyOperationType.REMOVE, "oppositeDirection" : true, "depth" : 1.5 * mm});
        }
        {
            var Q0;
            Q0=makeQuery(id+"F13.boolean.opBoolean","COPY",FACE,{"derivedFrom":makeQuery(id+"F13.opExtrude","CAP_FACE",FACE,{"disambiguationData":[OSD([sQuery(id+"F12.wireOp",EDGE,"E34"),sQuery(id+"F12.wireOp",EDGE,"E35.0")])],"isStart":false})});
            var sketch = newSketch(context, id + "F14", { "sketchPlane" : qUnion([Q0])});
            skLineSegment(sketch, "E36.left", {"start": v(-1, 3.23) * mm, "end": v(-1, 6.79) * mm});
            skLineSegment(sketch, "E36.right", {"start": v(1, 3.23) * mm, "end": v(1, 6.79) * mm});
            skArc(sketch, "E37.0", {"start": v(1, 6.79) * mm, "mid": v(0, 6.86) * mm, "end": v(-1, 6.79) * mm});
            skLineSegment(sketch, "E38", {"start": v(-1, 3.23) * mm, "end": v(1, 3.23) * mm});
            skSolve(sketch);
        }
        {
            var Q0;
            {var subQ0=sQuery(id+"F14.wireOp",EDGE,"E36.left");Q0=makeQuery(id+"F14.imprint","IMPRINT",FACE,{"disambiguationData":[TD([[makeQuery(id+"F14.imprint","IMPRINT",EDGE,{"derivedFrom":subQ0}),-1.0]])]});}
            extrude(context, id + "F15", {"entities" : qUnion([Q0]), "operationType" : NewBodyOperationType.ADD, "depth" : 4.5 * mm});
        }
        {
            var Q0;
            Q0=makeQuery(id+"F1.opRevolve","SWEPT_FACE",FACE,{"disambiguationData":[OSD([sQuery(id+"F0.wireOp",EDGE,"E7")])]});
            var sketch = newSketch(context, id + "F16", { "sketchPlane" : qUnion([Q0])});
            skCircle(sketch, "E39", {"center": v(0, 0) * mm, "radius": 3 * mm});
            skCircle(sketch, "E40", {"center": v(0, 0) * mm, "radius": 5 * mm});
            skSolve(sketch);
        }
        {
            var Q0;
            Q0=makeQuery(id+"F16.imprint","IMPRINT",FACE,{"disambiguationData":[TD([[makeQuery(id+"F16.imprint","IMPRINT",EDGE,{"derivedFrom":sQuery(id+"F16.wireOp",EDGE,"E40")}),1.0]])]});
            extrude(context, id + "F17", {"entities" : qUnion([Q0]), "depth" : 2.75 * mm});
        }
        {
            var Q0;
            Q0=makeQuery(id+"F1.opRevolve","SWEPT_FACE",FACE,{"disambiguationData":[OSD([sQuery(id+"F0.wireOp",EDGE,"E10")])]});
            var sketch = newSketch(context, id + "F18", { "sketchPlane" : qUnion([Q0])});
            skCircle(sketch, "E41", {"center": v(0, 0) * mm, "radius": 1.3 * mm});
            skSolve(sketch);
        }
        {
            var Q0;
            Q0=makeQuery(id+"F18.imprint","IMPRINT",FACE,{"disambiguationData":[TD([[makeQuery(id+"F18.imprint","IMPRINT",EDGE,{"derivedFrom":sQuery(id+"F18.wireOp",EDGE,"E41")}),1.0]])]});
            extrude(context, id + "F19", {"entities" : qUnion([Q0]), "operationType" : NewBodyOperationType.REMOVE, "oppositeDirection" : true, "depth" : 11 * mm});
        }
        {
            var Q0;
            Q0=makeQuery(id+"F17.opExtrude","CAP_FACE",FACE,{"disambiguationData":[OSD([sQuery(id+"F0.wireOp",EDGE,"E6"),sQuery(id+"F0.wireOp",EDGE,"E7"),sQuery(id+"F16.wireOp",EDGE,"E40")])],"isStart":true});
            var sketch = newSketch(context, id + "F20", { "sketchPlane" : qUnion([Q0])});
            skLineSegment(sketch, "E42.bottom", {"start": v(-22.5, 22.5) * mm, "end": v(22.5, 22.5) * mm});
            skLineSegment(sketch, "E42.top", {"start": v(-22.5, -22.5) * mm, "end": v(22.5, -22.5) * mm});
            skLineSegment(sketch, "E42.left", {"start": v(-22.5, 22.5) * mm, "end": v(-22.5, -22.5) * mm});
            skLineSegment(sketch, "E42.right", {"start": v(22.5, 22.5) * mm, "end": v(22.5, -22.5) * mm});
            skPoint(sketch, "E42.middle", {"position": v(0, 0) * mm});
            skCircle(sketch, "E43", {"center": v(0, 0) * mm, "radius": 11 * mm, "construction": true});
            skLineSegment(sketch, "E44", {"start": v(0, 0) * mm, "end": v(-1.53, 10.9) * mm, "construction": true});
            skCircle(sketch, "E45", {"center": v(-1.53, 10.9) * mm, "radius": 9 * mm, "construction": true});
            skCircle(sketch, "E46", {"center": v(-1.53, 10.9) * mm, "radius": 3.28 * mm, "construction": true});
            skCircle(sketch, "E47", {"center": v(-1.53, 10.9) * mm, "radius": 7.3 * mm, "construction": true});
            skCircle(sketch, "E48", {"center": v(7.38, 12.15) * mm, "radius": 5 * mm, "construction": true});
            skLineSegment(sketch, "E49", {"start": v(7.38, 12.15) * mm, "end": v(-1.53, 10.9) * mm, "construction": true});
            skCircle(sketch, "E50", {"center": v(7.38, 12.15) * mm, "radius": 2.5 * mm, "construction": true});
            skCircle(sketch, "E51", {"center": v(7.38, 12.15) * mm, "radius": 7.75 * mm, "construction": true});
            skCircle(sketch, "E52.0", {"center": v(0, 0) * mm, "radius": 5.25 * mm});
            skSolve(sketch);
        }
        {
            var Q0;
            Q0=makeQuery(id+"F20.imprint","IMPRINT",FACE,{"disambiguationData":[TD([[makeQuery(id+"F20.imprint","IMPRINT",EDGE,{"derivedFrom":sQuery(id+"F20.wireOp",EDGE,"E42.bottom")}),-1.0]])]});
            extrude(context, id + "F21", {"entities" : qUnion([Q0]), "oppositeDirection" : true, "depth" : 2 * mm});
        }
        {
            var Q0;
            Q0=qCreatedBy(makeId("Front.planeOp"),FACE);
            var sketch = newSketch(context, id + "F22", { "sketchPlane" : qUnion([Q0])});
            skLineSegment(sketch, "E53", {"start": v(5.25, 11.84) * mm, "end": v(5.25, 12.64) * mm});
            skLineSegment(sketch, "E54", {"start": v(5.25, 12.64) * mm, "end": v(4, 12.64) * mm});
            skLineSegment(sketch, "E55", {"start": v(4, 12.64) * mm, "end": v(4, 13.24) * mm});
            skLineSegment(sketch, "E56", {"start": v(4, 13.24) * mm, "end": v(7.25, 13.24) * mm});
            skLineSegment(sketch, "E57", {"start": v(7.25, 13.24) * mm, "end": v(7.25, 11.84) * mm});
            skLineSegment(sketch, "E58", {"start": v(7.25, 11.84) * mm, "end": v(5.25, 11.84) * mm});
            skSolve(sketch);
        }
        {
            var Q0;
            Q0=makeQuery(id+"F22.imprint","IMPRINT",FACE,{"disambiguationData":[TD([[makeQuery(id+"F22.imprint","IMPRINT",EDGE,{"derivedFrom":sQuery(id+"F22.wireOp",EDGE,"E53")}),-1.0]])]});
            var Q1;
            Q1=makeQuery(id+"F19.boolean.opBoolean","COPY",FACE,{"derivedFrom":makeQuery(id+"F19.opExtrude","SWEPT_FACE",FACE,{"disambiguationData":[OSD([sQuery(id+"F18.wireOp",EDGE,"E41")])]})});
            revolve(context, id + "F23", {"operationType" : NewBodyOperationType.ADD, "entities" : qUnion([Q0]), "axis" : qUnion([Q1]), "revolveType" : RevolveType.FULL});
        }
        {
            var Q0;
            Q0=makeQuery(id+"F1.opRevolve","SWEPT_FACE",FACE,{"disambiguationData":[OSD([sQuery(id+"F0.wireOp",EDGE,"E3")])]});
            var sketch = newSketch(context, id + "F24", { "sketchPlane" : qUnion([Q0])});
            skPoint(sketch, "E59", {"position": v(-1.52, 10.88) * mm});
            skCircle(sketch, "E60", {"center": v(-1.52, 10.88) * mm, "radius": 3.25 * mm});
            skLineSegment(sketch, "E61", {"start": v(-1.52, 10.88) * mm, "end": v(-1.52, 14.13) * mm, "construction": true});
            skLineSegment(sketch, "E62.1.0", {"start": v(-1.52, 10.88) * mm, "end": v(-3.28, 13.62) * mm, "construction": true});
            skLineSegment(sketch, "E62.2.0", {"start": v(-1.52, 10.88) * mm, "end": v(-4.48, 12.24) * mm, "construction": true});
            skLineSegment(sketch, "E62.3.0", {"start": v(-1.52, 10.88) * mm, "end": v(-4.74, 10.42) * mm, "construction": true});
            skLineSegment(sketch, "E62.4.0", {"start": v(-1.52, 10.88) * mm, "end": v(-3.98, 8.76) * mm, "construction": true});
            skLineSegment(sketch, "E62.5.0", {"start": v(-1.52, 10.88) * mm, "end": v(-2.44, 7.77) * mm, "construction": true});
            skLineSegment(sketch, "E62.6.0", {"start": v(-1.52, 10.88) * mm, "end": v(-0.6, 7.77) * mm, "construction": true});
            skLineSegment(sketch, "E62.7.0", {"start": v(-1.52, 10.88) * mm, "end": v(0.93, 8.76) * mm, "construction": true});
            skLineSegment(sketch, "E62.8.0", {"start": v(-1.52, 10.88) * mm, "end": v(1.7, 10.42) * mm, "construction": true});
            skLineSegment(sketch, "E62.9.0", {"start": v(-1.52, 10.88) * mm, "end": v(1.43, 12.24) * mm, "construction": true});
            skLineSegment(sketch, "E62.10.0", {"start": v(-1.52, 10.88) * mm, "end": v(0.24, 13.62) * mm, "construction": true});
            skArc(sketch, "E63", {"start": v(-1.28, 13.94) * mm, "mid": v(-1.36, 14.08) * mm, "end": v(-1.52, 14.13) * mm});
            skLineSegment(sketch, "E64", {"start": v(-1.52, 10.88) * mm, "end": v(-0.6, 14) * mm, "construction": true});
            skArc(sketch, "E65", {"start": v(-1.1, 13.11) * mm, "mid": v(-0.92, 12.92) * mm, "end": v(-0.68, 12.99) * mm});
            skArc(sketch, "E66.MirrorC", {"start": v(-0.08, 13.59) * mm, "mid": v(0.07, 13.66) * mm, "end": v(0.24, 13.62) * mm});
            skLineSegment(sketch, "E67", {"start": v(-1.1, 13.11) * mm, "end": v(-1.28, 13.94) * mm});
            skLineSegment(sketch, "E68.MirrorCS", {"start": v(-0.68, 12.99) * mm, "end": v(-0.08, 13.59) * mm});
            skArc(sketch, "E69.1.0", {"start": v(-1.77, 13.94) * mm, "mid": v(-1.68, 14.08) * mm, "end": v(-1.52, 14.13) * mm});
            skLineSegment(sketch, "E69.1.1", {"start": v(-1.95, 13.11) * mm, "end": v(-1.77, 13.94) * mm});
            skArc(sketch, "E69.1.2", {"start": v(-2.37, 12.99) * mm, "mid": v(-2.12, 12.92) * mm, "end": v(-1.95, 13.11) * mm});
            skLineSegment(sketch, "E69.1.3", {"start": v(-2.37, 12.99) * mm, "end": v(-2.97, 13.59) * mm});
            skArc(sketch, "E69.1.4", {"start": v(-2.97, 13.59) * mm, "mid": v(-3.12, 13.66) * mm, "end": v(-3.28, 13.62) * mm});
            skArc(sketch, "E69.2.0", {"start": v(-3.38, 13.32) * mm, "mid": v(-3.38, 13.49) * mm, "end": v(-3.28, 13.62) * mm});
            skLineSegment(sketch, "E69.2.1", {"start": v(-3.08, 12.53) * mm, "end": v(-3.38, 13.32) * mm});
            skArc(sketch, "E69.2.2", {"start": v(-3.37, 12.2) * mm, "mid": v(-3.13, 12.28) * mm, "end": v(-3.08, 12.53) * mm});
            skLineSegment(sketch, "E69.2.3", {"start": v(-3.37, 12.2) * mm, "end": v(-4.2, 12.38) * mm});
            skArc(sketch, "E69.2.4", {"start": v(-4.2, 12.38) * mm, "mid": v(-4.36, 12.35) * mm, "end": v(-4.48, 12.24) * mm});
            skArc(sketch, "E69.3.0", {"start": v(-4.4, 11.93) * mm, "mid": v(-4.5, 12.07) * mm, "end": v(-4.48, 12.24) * mm});
            skLineSegment(sketch, "E69.3.1", {"start": v(-3.72, 11.42) * mm, "end": v(-4.4, 11.93) * mm});
            skArc(sketch, "E69.3.2", {"start": v(-3.78, 10.99) * mm, "mid": v(-3.63, 11.19) * mm, "end": v(-3.72, 11.42) * mm});
            skLineSegment(sketch, "E69.3.3", {"start": v(-3.78, 10.99) * mm, "end": v(-4.58, 10.7) * mm});
            skArc(sketch, "E69.3.4", {"start": v(-4.58, 10.7) * mm, "mid": v(-4.7, 10.59) * mm, "end": v(-4.74, 10.42) * mm});
            skArc(sketch, "E69.4.0", {"start": v(-4.5, 10.2) * mm, "mid": v(-4.66, 10.28) * mm, "end": v(-4.74, 10.42) * mm});
            skLineSegment(sketch, "E69.4.1", {"start": v(-3.66, 10.15) * mm, "end": v(-4.5, 10.2) * mm});
            skArc(sketch, "E69.4.2", {"start": v(-3.48, 9.75) * mm, "mid": v(-3.45, 10) * mm, "end": v(-3.66, 10.15) * mm});
            skLineSegment(sketch, "E69.4.3", {"start": v(-3.48, 9.75) * mm, "end": v(-3.99, 9.07) * mm});
            skArc(sketch, "E69.4.4", {"start": v(-3.99, 9.07) * mm, "mid": v(-4.04, 8.91) * mm, "end": v(-3.98, 8.76) * mm});
            skArc(sketch, "E69.5.0", {"start": v(-3.67, 8.7) * mm, "mid": v(-3.83, 8.67) * mm, "end": v(-3.98, 8.76) * mm});
            skLineSegment(sketch, "E69.5.1", {"start": v(-2.93, 9.1) * mm, "end": v(-3.67, 8.7) * mm});
            skArc(sketch, "E69.5.2", {"start": v(-2.56, 8.87) * mm, "mid": v(-2.67, 9.1) * mm, "end": v(-2.93, 9.1) * mm});
            skLineSegment(sketch, "E69.5.3", {"start": v(-2.56, 8.87) * mm, "end": v(-2.62, 8.02) * mm});
            skArc(sketch, "E69.5.4", {"start": v(-2.62, 8.02) * mm, "mid": v(-2.57, 7.86) * mm, "end": v(-2.44, 7.77) * mm});
            skArc(sketch, "E69.6.0", {"start": v(-2.15, 7.89) * mm, "mid": v(-2.27, 7.78) * mm, "end": v(-2.44, 7.77) * mm});
            skLineSegment(sketch, "E69.6.1", {"start": v(-1.74, 8.63) * mm, "end": v(-2.15, 7.89) * mm});
            skArc(sketch, "E69.6.2", {"start": v(-1.3, 8.63) * mm, "mid": v(-1.52, 8.76) * mm, "end": v(-1.74, 8.63) * mm});
            skLineSegment(sketch, "E69.6.3", {"start": v(-1.3, 8.63) * mm, "end": v(-0.9, 7.89) * mm});
            skArc(sketch, "E69.6.4", {"start": v(-0.9, 7.89) * mm, "mid": v(-0.77, 7.78) * mm, "end": v(-0.6, 7.77) * mm});
            skArc(sketch, "E69.7.0", {"start": v(-0.43, 8.02) * mm, "mid": v(-0.47, 7.86) * mm, "end": v(-0.6, 7.77) * mm});
            skLineSegment(sketch, "E69.7.1", {"start": v(-0.49, 8.87) * mm, "end": v(-0.43, 8.02) * mm});
            skArc(sketch, "E69.7.2", {"start": v(-0.12, 9.1) * mm, "mid": v(-0.37, 9.1) * mm, "end": v(-0.49, 8.87) * mm});
            skLineSegment(sketch, "E69.7.3", {"start": v(-0.12, 9.1) * mm, "end": v(0.63, 8.7) * mm});
            skArc(sketch, "E69.7.4", {"start": v(0.63, 8.7) * mm, "mid": v(0.8, 8.67) * mm, "end": v(0.93, 8.76) * mm});
            skArc(sketch, "E69.8.0", {"start": v(0.95, 9.07) * mm, "mid": v(1, 8.91) * mm, "end": v(0.93, 8.76) * mm});
            skLineSegment(sketch, "E69.8.1", {"start": v(0.44, 9.75) * mm, "end": v(0.95, 9.07) * mm});
            skArc(sketch, "E69.8.2", {"start": v(0.62, 10.15) * mm, "mid": v(0.41, 10) * mm, "end": v(0.44, 9.75) * mm});
            skLineSegment(sketch, "E69.8.3", {"start": v(0.62, 10.15) * mm, "end": v(1.47, 10.2) * mm});
            skArc(sketch, "E69.8.4", {"start": v(1.47, 10.2) * mm, "mid": v(1.62, 10.28) * mm, "end": v(1.7, 10.42) * mm});
            skArc(sketch, "E69.9.0", {"start": v(1.54, 10.7) * mm, "mid": v(1.66, 10.59) * mm, "end": v(1.7, 10.42) * mm});
            skLineSegment(sketch, "E69.9.1", {"start": v(0.74, 10.99) * mm, "end": v(1.54, 10.7) * mm});
            skArc(sketch, "E69.9.2", {"start": v(0.68, 11.42) * mm, "mid": v(0.58, 11.19) * mm, "end": v(0.74, 10.99) * mm});
            skLineSegment(sketch, "E69.9.3", {"start": v(0.68, 11.42) * mm, "end": v(1.36, 11.93) * mm});
            skArc(sketch, "E69.9.4", {"start": v(1.36, 11.93) * mm, "mid": v(1.45, 12.07) * mm, "end": v(1.43, 12.24) * mm});
            skArc(sketch, "E69.10.0", {"start": v(1.15, 12.38) * mm, "mid": v(1.32, 12.35) * mm, "end": v(1.43, 12.24) * mm});
            skLineSegment(sketch, "E69.10.1", {"start": v(0.33, 12.2) * mm, "end": v(1.15, 12.38) * mm});
            skArc(sketch, "E69.10.2", {"start": v(0.04, 12.53) * mm, "mid": v(0.08, 12.28) * mm, "end": v(0.33, 12.2) * mm});
            skLineSegment(sketch, "E69.10.3", {"start": v(0.04, 12.53) * mm, "end": v(0.33, 13.32) * mm});
            skArc(sketch, "E69.10.4", {"start": v(0.33, 13.32) * mm, "mid": v(0.34, 13.49) * mm, "end": v(0.24, 13.62) * mm});
            skCircle(sketch, "E70", {"center": v(-1.52, 10.88) * mm, "radius": 0.8 * mm});
            skSolve(sketch);
        }
        {
            var Q0;
            Q0=makeQuery(id+"F24.imprint","IMPRINT",FACE,{"disambiguationData":[TD([[makeQuery(id+"F24.imprint","IMPRINT",EDGE,{"derivedFrom":sQuery(id+"F24.wireOp",EDGE,"E63")}),1.0]])]});
            extrude(context, id + "F25", {"entities" : qUnion([Q0]), "oppositeDirection" : true, "depth" : 5.5 * mm});
        }
        {
            var Q0;
            Q0=makeQuery(id+"F25.opExtrude","CAP_FACE",FACE,{"disambiguationData":[OSD([sQuery(id+"F0.wireOp",EDGE,"E3"),sQuery(id+"F4.wireOp",EDGE,"E27.16.1"),sQuery(id+"F24.wireOp",EDGE,"E63"),sQuery(id+"F24.wireOp",EDGE,"E65"),sQuery(id+"F24.wireOp",EDGE,"E66.MirrorC"),sQuery(id+"F24.wireOp",EDGE,"E67"),sQuery(id+"F24.wireOp",EDGE,"E68.MirrorCS"),sQuery(id+"F24.wireOp",EDGE,"E69.1.0"),sQuery(id+"F24.wireOp",EDGE,"E69.1.1"),sQuery(id+"F24.wireOp",EDGE,"E69.1.2"),sQuery(id+"F24.wireOp",EDGE,"E69.1.3"),sQuery(id+"F24.wireOp",EDGE,"E69.1.4"),sQuery(id+"F24.wireOp",EDGE,"E69.2.0"),sQuery(id+"F24.wireOp",EDGE,"E69.2.1"),sQuery(id+"F24.wireOp",EDGE,"E69.2.2"),sQuery(id+"F24.wireOp",EDGE,"E69.2.3"),sQuery(id+"F24.wireOp",EDGE,"E69.2.4"),sQuery(id+"F24.wireOp",EDGE,"E69.3.0"),sQuery(id+"F24.wireOp",EDGE,"E69.3.1"),sQuery(id+"F24.wireOp",EDGE,"E69.3.2"),sQuery(id+"F24.wireOp",EDGE,"E69.3.3"),sQuery(id+"F24.wireOp",EDGE,"E69.3.4"),sQuery(id+"F24.wireOp",EDGE,"E69.4.0"),sQuery(id+"F24.wireOp",EDGE,"E69.4.1"),sQuery(id+"F24.wireOp",EDGE,"E69.4.2"),sQuery(id+"F24.wireOp",EDGE,"E69.4.3"),sQuery(id+"F24.wireOp",EDGE,"E69.4.4"),sQuery(id+"F24.wireOp",EDGE,"E69.5.0"),sQuery(id+"F24.wireOp",EDGE,"E69.5.1"),sQuery(id+"F24.wireOp",EDGE,"E69.5.2"),sQuery(id+"F24.wireOp",EDGE,"E69.5.3"),sQuery(id+"F24.wireOp",EDGE,"E69.5.4"),sQuery(id+"F24.wireOp",EDGE,"E69.6.0"),sQuery(id+"F24.wireOp",EDGE,"E69.6.1"),sQuery(id+"F24.wireOp",EDGE,"E69.6.2"),sQuery(id+"F24.wireOp",EDGE,"E69.6.3"),sQuery(id+"F24.wireOp",EDGE,"E69.6.4"),sQuery(id+"F24.wireOp",EDGE,"E69.7.0"),sQuery(id+"F24.wireOp",EDGE,"E69.7.1"),sQuery(id+"F24.wireOp",EDGE,"E69.7.2"),sQuery(id+"F24.wireOp",EDGE,"E69.7.3"),sQuery(id+"F24.wireOp",EDGE,"E69.7.4"),sQuery(id+"F24.wireOp",EDGE,"E69.8.0"),sQuery(id+"F24.wireOp",EDGE,"E69.8.1"),sQuery(id+"F24.wireOp",EDGE,"E69.8.2"),sQuery(id+"F24.wireOp",EDGE,"E69.8.3"),sQuery(id+"F24.wireOp",EDGE,"E69.8.4"),sQuery(id+"F24.wireOp",EDGE,"E69.9.0"),sQuery(id+"F24.wireOp",EDGE,"E69.9.1"),sQuery(id+"F24.wireOp",EDGE,"E69.9.2"),sQuery(id+"F24.wireOp",EDGE,"E69.9.3"),sQuery(id+"F24.wireOp",EDGE,"E69.9.4"),sQuery(id+"F24.wireOp",EDGE,"E69.10.0"),sQuery(id+"F24.wireOp",EDGE,"E69.10.1"),sQuery(id+"F24.wireOp",EDGE,"E69.10.2"),sQuery(id+"F24.wireOp",EDGE,"E69.10.3"),sQuery(id+"F24.wireOp",EDGE,"E69.10.4"),sQuery(id+"F24.wireOp",EDGE,"E70")])],"isStart":false});
            var sketch = newSketch(context, id + "F26", { "sketchPlane" : qUnion([Q0])});
            skCircle(sketch, "E71", {"center": v(-1.52, -10.88) * mm, "radius": 7.38 * mm});
            skCircle(sketch, "E72.0", {"center": v(-1.52, -10.88) * mm, "radius": 0.8 * mm});
            skSolve(sketch);
        }
        {
            var Q0;
            Q0 = qSketchRegion(id + "F26", true);
            extrude(context, id + "F27", {"entities" : qUnion([Q0]), "operationType" : NewBodyOperationType.ADD, "depth" : 2.5 * mm});
        }
        {
            var Q0;
            Q0=makeQuery(id+"F27.opExtrude","CAP_FACE",FACE,{"disambiguationData":[OSD([sQuery(id+"F26.wireOp",EDGE,"E71"),sQuery(id+"F26.wireOp",EDGE,"E72.0")])],"isStart":false});
            var sketch = newSketch(context, id + "F28", { "sketchPlane" : qUnion([Q0])});
            skCircle(sketch, "E73", {"center": v(-1.52, -10.88) * mm, "radius": 5.5 * mm});
            skSolve(sketch);
        }
        {
            var Q0;
            Q0=makeQuery(id+"F28.imprint","IMPRINT",FACE,{"disambiguationData":[TD([[makeQuery(id+"F28.imprint","IMPRINT",EDGE,{"derivedFrom":sQuery(id+"F28.wireOp",EDGE,"E73")}),1.0]])]});
            extrude(context, id + "F29", {"entities" : qUnion([Q0]), "operationType" : NewBodyOperationType.REMOVE, "oppositeDirection" : true, "depth" : 0.8 * mm});
        }
        {
            var Q0;
            Q0=makeQuery(id+"F29.boolean.opBoolean","COPY",EDGE,{"derivedFrom":makeQuery(id+"F29.opExtrude","CAP_EDGE",EDGE,{"disambiguationData":[OSD([sQuery(id+"F28.wireOp",EDGE,"E73")])],"isStart":false})});
            chamfer(context, id + "F30", {"entities" : qUnion([Q0]), "width" : .8 * mm, "tangentPropagation" : true});
        }
        {
            var Q0;
            Q0=makeQuery(id+"F27.opExtrude","CAP_FACE",FACE,{"disambiguationData":[OSD([sQuery(id+"F26.wireOp",EDGE,"E71"),sQuery(id+"F26.wireOp",EDGE,"E72.0")])],"isStart":false});
            var sketch = newSketch(context, id + "F31", { "sketchPlane" : qUnion([Q0])});
            skLineSegment(sketch, "E74", {"start": v(-1.52, -10.88) * mm, "end": v(-8.9, -10.88) * mm, "construction": true});
            skLineSegment(sketch, "E75", {"start": v(-1.52, -10.88) * mm, "end": v(-8.87, -11.53) * mm, "construction": true});
            skLineSegment(sketch, "E76.MirrorCS", {"start": v(-1.52, -10.88) * mm, "end": v(-8.87, -10.24) * mm, "construction": true});
            skLineSegment(sketch, "E77", {"start": v(-7.9, -10.88) * mm, "end": v(-8.87, -11.53) * mm});
            skLineSegment(sketch, "E78.MirrorCS", {"start": v(-7.9, -10.88) * mm, "end": v(-8.87, -10.24) * mm});
            skLineSegment(sketch, "E79.1.0", {"start": v(-7.8, -12) * mm, "end": v(-8.65, -12.8) * mm});
            skLineSegment(sketch, "E79.1.1", {"start": v(-7.8, -12) * mm, "end": v(-8.87, -11.53) * mm});
            skLineSegment(sketch, "E79.2.0", {"start": v(-7.51, -13.07) * mm, "end": v(-8.2, -14) * mm});
            skLineSegment(sketch, "E79.2.1", {"start": v(-7.51, -13.07) * mm, "end": v(-8.65, -12.8) * mm});
            skLineSegment(sketch, "E79.3.0", {"start": v(-7.04, -14.07) * mm, "end": v(-7.56, -15.12) * mm});
            skLineSegment(sketch, "E79.3.1", {"start": v(-7.04, -14.07) * mm, "end": v(-8.2, -14) * mm});
            skLineSegment(sketch, "E79.4.0", {"start": v(-6.4, -14.98) * mm, "end": v(-6.74, -16.1) * mm});
            skLineSegment(sketch, "E79.4.1", {"start": v(-6.4, -14.98) * mm, "end": v(-7.56, -15.12) * mm});
            skLineSegment(sketch, "E79.5.0", {"start": v(-5.62, -15.77) * mm, "end": v(-5.75, -16.93) * mm});
            skLineSegment(sketch, "E79.5.1", {"start": v(-5.62, -15.77) * mm, "end": v(-6.74, -16.1) * mm});
            skLineSegment(sketch, "E79.6.0", {"start": v(-4.7, -16.4) * mm, "end": v(-4.64, -17.57) * mm});
            skLineSegment(sketch, "E79.6.1", {"start": v(-4.7, -16.4) * mm, "end": v(-5.75, -16.93) * mm});
            skLineSegment(sketch, "E79.7.0", {"start": v(-3.7, -16.88) * mm, "end": v(-3.43, -18) * mm});
            skLineSegment(sketch, "E79.7.1", {"start": v(-3.7, -16.88) * mm, "end": v(-4.64, -17.57) * mm});
            skLineSegment(sketch, "E79.8.0", {"start": v(-2.63, -17.16) * mm, "end": v(-2.16, -18.23) * mm});
            skLineSegment(sketch, "E79.8.1", {"start": v(-2.63, -17.16) * mm, "end": v(-3.43, -18) * mm});
            skLineSegment(sketch, "E79.9.0", {"start": v(-1.52, -17.26) * mm, "end": v(-0.88, -18.23) * mm});
            skLineSegment(sketch, "E79.9.1", {"start": v(-1.52, -17.26) * mm, "end": v(-2.16, -18.23) * mm});
            skLineSegment(sketch, "E79.10.0", {"start": v(-0.41, -17.16) * mm, "end": v(0.39, -18) * mm});
            skLineSegment(sketch, "E79.10.1", {"start": v(-0.41, -17.16) * mm, "end": v(-0.88, -18.23) * mm});
            skLineSegment(sketch, "E79.11.0", {"start": v(0.66, -16.88) * mm, "end": v(1.6, -17.57) * mm});
            skLineSegment(sketch, "E79.11.1", {"start": v(0.66, -16.88) * mm, "end": v(0.39, -18) * mm});
            skLineSegment(sketch, "E79.12.0", {"start": v(1.67, -16.4) * mm, "end": v(2.7, -16.93) * mm});
            skLineSegment(sketch, "E79.12.1", {"start": v(1.67, -16.4) * mm, "end": v(1.6, -17.57) * mm});
            skLineSegment(sketch, "E79.13.0", {"start": v(2.58, -15.77) * mm, "end": v(3.7, -16.1) * mm});
            skLineSegment(sketch, "E79.13.1", {"start": v(2.58, -15.77) * mm, "end": v(2.7, -16.93) * mm});
            skLineSegment(sketch, "E79.14.0", {"start": v(3.36, -14.98) * mm, "end": v(4.52, -15.12) * mm});
            skLineSegment(sketch, "E79.14.1", {"start": v(3.36, -14.98) * mm, "end": v(3.7, -16.1) * mm});
            skLineSegment(sketch, "E79.15.0", {"start": v(4, -14.07) * mm, "end": v(5.16, -14) * mm});
            skLineSegment(sketch, "E79.15.1", {"start": v(4, -14.07) * mm, "end": v(4.52, -15.12) * mm});
            skLineSegment(sketch, "E79.16.0", {"start": v(4.47, -13.07) * mm, "end": v(5.6, -12.8) * mm});
            skLineSegment(sketch, "E79.16.1", {"start": v(4.47, -13.07) * mm, "end": v(5.16, -14) * mm});
            skLineSegment(sketch, "E79.17.0", {"start": v(4.76, -12) * mm, "end": v(5.83, -11.53) * mm});
            skLineSegment(sketch, "E79.17.1", {"start": v(4.76, -12) * mm, "end": v(5.6, -12.8) * mm});
            skLineSegment(sketch, "E79.18.0", {"start": v(4.85, -10.88) * mm, "end": v(5.83, -10.24) * mm});
            skLineSegment(sketch, "E79.18.1", {"start": v(4.85, -10.88) * mm, "end": v(5.83, -11.53) * mm});
            skLineSegment(sketch, "E79.19.0", {"start": v(4.76, -9.78) * mm, "end": v(5.6, -8.98) * mm});
            skLineSegment(sketch, "E79.19.1", {"start": v(4.76, -9.78) * mm, "end": v(5.83, -10.24) * mm});
            skLineSegment(sketch, "E79.20.0", {"start": v(4.47, -8.7) * mm, "end": v(5.16, -7.77) * mm});
            skLineSegment(sketch, "E79.20.1", {"start": v(4.47, -8.7) * mm, "end": v(5.6, -8.98) * mm});
            skLineSegment(sketch, "E79.21.0", {"start": v(4, -7.7) * mm, "end": v(4.52, -6.65) * mm});
            skLineSegment(sketch, "E79.21.1", {"start": v(4, -7.7) * mm, "end": v(5.16, -7.77) * mm});
            skLineSegment(sketch, "E79.22.0", {"start": v(3.36, -6.79) * mm, "end": v(3.7, -5.67) * mm});
            skLineSegment(sketch, "E79.22.1", {"start": v(3.36, -6.79) * mm, "end": v(4.52, -6.65) * mm});
            skLineSegment(sketch, "E79.23.0", {"start": v(2.58, -6) * mm, "end": v(2.7, -4.84) * mm});
            skLineSegment(sketch, "E79.23.1", {"start": v(2.58, -6) * mm, "end": v(3.7, -5.67) * mm});
            skLineSegment(sketch, "E79.24.0", {"start": v(1.67, -5.36) * mm, "end": v(1.6, -4.2) * mm});
            skLineSegment(sketch, "E79.24.1", {"start": v(1.67, -5.36) * mm, "end": v(2.7, -4.84) * mm});
            skLineSegment(sketch, "E79.25.0", {"start": v(0.66, -4.9) * mm, "end": v(0.39, -3.76) * mm});
            skLineSegment(sketch, "E79.25.1", {"start": v(0.66, -4.9) * mm, "end": v(1.6, -4.2) * mm});
            skLineSegment(sketch, "E79.26.0", {"start": v(-0.41, -4.6) * mm, "end": v(-0.88, -3.54) * mm});
            skLineSegment(sketch, "E79.26.1", {"start": v(-0.41, -4.6) * mm, "end": v(0.39, -3.76) * mm});
            skLineSegment(sketch, "E79.27.0", {"start": v(-1.52, -4.5) * mm, "end": v(-2.16, -3.54) * mm});
            skLineSegment(sketch, "E79.27.1", {"start": v(-1.52, -4.5) * mm, "end": v(-0.88, -3.54) * mm});
            skLineSegment(sketch, "E79.28.0", {"start": v(-2.63, -4.6) * mm, "end": v(-3.43, -3.76) * mm});
            skLineSegment(sketch, "E79.28.1", {"start": v(-2.63, -4.6) * mm, "end": v(-2.16, -3.54) * mm});
            skLineSegment(sketch, "E79.29.0", {"start": v(-3.7, -4.9) * mm, "end": v(-4.64, -4.2) * mm});
            skLineSegment(sketch, "E79.29.1", {"start": v(-3.7, -4.9) * mm, "end": v(-3.43, -3.76) * mm});
            skLineSegment(sketch, "E79.30.0", {"start": v(-4.7, -5.36) * mm, "end": v(-5.75, -4.84) * mm});
            skLineSegment(sketch, "E79.30.1", {"start": v(-4.7, -5.36) * mm, "end": v(-4.64, -4.2) * mm});
            skLineSegment(sketch, "E79.31.0", {"start": v(-5.62, -6) * mm, "end": v(-6.74, -5.67) * mm});
            skLineSegment(sketch, "E79.31.1", {"start": v(-5.62, -6) * mm, "end": v(-5.75, -4.84) * mm});
            skLineSegment(sketch, "E79.32.0", {"start": v(-6.4, -6.79) * mm, "end": v(-7.56, -6.65) * mm});
            skLineSegment(sketch, "E79.32.1", {"start": v(-6.4, -6.79) * mm, "end": v(-6.74, -5.67) * mm});
            skLineSegment(sketch, "E79.33.0", {"start": v(-7.04, -7.7) * mm, "end": v(-8.2, -7.77) * mm});
            skLineSegment(sketch, "E79.33.1", {"start": v(-7.04, -7.7) * mm, "end": v(-7.56, -6.65) * mm});
            skLineSegment(sketch, "E79.34.0", {"start": v(-7.51, -8.7) * mm, "end": v(-8.65, -8.98) * mm});
            skLineSegment(sketch, "E79.34.1", {"start": v(-7.51, -8.7) * mm, "end": v(-8.2, -7.77) * mm});
            skLineSegment(sketch, "E79.35.0", {"start": v(-7.8, -9.78) * mm, "end": v(-8.87, -10.24) * mm});
            skLineSegment(sketch, "E79.35.1", {"start": v(-7.8, -9.78) * mm, "end": v(-8.65, -8.98) * mm});
            skPoint(sketch, "E79.center", {"position": v(-1.52, -10.88) * mm});
            skSolve(sketch);
        }
        {
            var Q0;
            {var subQ0=sQuery(id+"F31.wireOp",EDGE,"E79.5.0");Q0=makeQuery(id+"F31.imprint","IMPRINT",FACE,{"disambiguationData":[TD([[makeQuery(id+"F31.imprint","IMPRINT",EDGE,{"derivedFrom":subQ0}),-1.0]])]});}
            var Q1;
            {var subQ0=sQuery(id+"F31.wireOp",EDGE,"E79.4.0");Q1=makeQuery(id+"F31.imprint","IMPRINT",FACE,{"disambiguationData":[TD([[makeQuery(id+"F31.imprint","IMPRINT",EDGE,{"derivedFrom":subQ0}),-1.0]])]});}
            var Q2;
            {var subQ0=sQuery(id+"F31.wireOp",EDGE,"E79.3.0");Q2=makeQuery(id+"F31.imprint","IMPRINT",FACE,{"disambiguationData":[TD([[makeQuery(id+"F31.imprint","IMPRINT",EDGE,{"derivedFrom":subQ0}),-1.0]])]});}
            var Q3;
            {var subQ0=sQuery(id+"F31.wireOp",EDGE,"E79.2.0");Q3=makeQuery(id+"F31.imprint","IMPRINT",FACE,{"disambiguationData":[TD([[makeQuery(id+"F31.imprint","IMPRINT",EDGE,{"derivedFrom":subQ0}),-1.0]])]});}
            var Q4;
            {var subQ0=sQuery(id+"F31.wireOp",EDGE,"E79.1.0");Q4=makeQuery(id+"F31.imprint","IMPRINT",FACE,{"disambiguationData":[TD([[makeQuery(id+"F31.imprint","IMPRINT",EDGE,{"derivedFrom":subQ0}),-1.0]])]});}
            var Q5;
            {var subQ0=sQuery(id+"F31.wireOp",EDGE,"E77");Q5=makeQuery(id+"F31.imprint","IMPRINT",FACE,{"disambiguationData":[TD([[makeQuery(id+"F31.imprint","IMPRINT",EDGE,{"derivedFrom":subQ0}),-1.0]])]});}
            var Q6;
            {var subQ0=sQuery(id+"F31.wireOp",EDGE,"E79.35.0");Q6=makeQuery(id+"F31.imprint","IMPRINT",FACE,{"disambiguationData":[TD([[makeQuery(id+"F31.imprint","IMPRINT",EDGE,{"derivedFrom":subQ0}),-1.0]])]});}
            var Q7;
            {var subQ0=sQuery(id+"F31.wireOp",EDGE,"E79.34.0");Q7=makeQuery(id+"F31.imprint","IMPRINT",FACE,{"disambiguationData":[TD([[makeQuery(id+"F31.imprint","IMPRINT",EDGE,{"derivedFrom":subQ0}),-1.0]])]});}
            var Q8;
            {var subQ0=sQuery(id+"F31.wireOp",EDGE,"E79.33.0");Q8=makeQuery(id+"F31.imprint","IMPRINT",FACE,{"disambiguationData":[TD([[makeQuery(id+"F31.imprint","IMPRINT",EDGE,{"derivedFrom":subQ0}),-1.0]])]});}
            var Q9;
            {var subQ0=sQuery(id+"F31.wireOp",EDGE,"E79.32.0");Q9=makeQuery(id+"F31.imprint","IMPRINT",FACE,{"disambiguationData":[TD([[makeQuery(id+"F31.imprint","IMPRINT",EDGE,{"derivedFrom":subQ0}),-1.0]])]});}
            var Q10;
            {var subQ0=sQuery(id+"F31.wireOp",EDGE,"E79.31.0");Q10=makeQuery(id+"F31.imprint","IMPRINT",FACE,{"disambiguationData":[TD([[makeQuery(id+"F31.imprint","IMPRINT",EDGE,{"derivedFrom":subQ0}),-1.0]])]});}
            var Q11;
            {var subQ0=sQuery(id+"F31.wireOp",EDGE,"E79.30.0");Q11=makeQuery(id+"F31.imprint","IMPRINT",FACE,{"disambiguationData":[TD([[makeQuery(id+"F31.imprint","IMPRINT",EDGE,{"derivedFrom":subQ0}),-1.0]])]});}
            var Q12;
            {var subQ0=sQuery(id+"F31.wireOp",EDGE,"E79.29.0");Q12=makeQuery(id+"F31.imprint","IMPRINT",FACE,{"disambiguationData":[TD([[makeQuery(id+"F31.imprint","IMPRINT",EDGE,{"derivedFrom":subQ0}),-1.0]])]});}
            var Q13;
            {var subQ0=sQuery(id+"F31.wireOp",EDGE,"E79.6.0");Q13=makeQuery(id+"F31.imprint","IMPRINT",FACE,{"disambiguationData":[TD([[makeQuery(id+"F31.imprint","IMPRINT",EDGE,{"derivedFrom":subQ0}),-1.0]])]});}
            var Q14;
            {var subQ0=sQuery(id+"F31.wireOp",EDGE,"E79.7.0");Q14=makeQuery(id+"F31.imprint","IMPRINT",FACE,{"disambiguationData":[TD([[makeQuery(id+"F31.imprint","IMPRINT",EDGE,{"derivedFrom":subQ0}),-1.0]])]});}
            var Q15;
            {var subQ0=sQuery(id+"F31.wireOp",EDGE,"E79.8.0");Q15=makeQuery(id+"F31.imprint","IMPRINT",FACE,{"disambiguationData":[TD([[makeQuery(id+"F31.imprint","IMPRINT",EDGE,{"derivedFrom":subQ0}),-1.0]])]});}
            var Q16;
            {var subQ0=sQuery(id+"F31.wireOp",EDGE,"E79.9.0");Q16=makeQuery(id+"F31.imprint","IMPRINT",FACE,{"disambiguationData":[TD([[makeQuery(id+"F31.imprint","IMPRINT",EDGE,{"derivedFrom":subQ0}),-1.0]])]});}
            var Q17;
            {var subQ0=sQuery(id+"F31.wireOp",EDGE,"E79.10.0");Q17=makeQuery(id+"F31.imprint","IMPRINT",FACE,{"disambiguationData":[TD([[makeQuery(id+"F31.imprint","IMPRINT",EDGE,{"derivedFrom":subQ0}),-1.0]])]});}
            var Q18;
            {var subQ0=sQuery(id+"F31.wireOp",EDGE,"E79.11.0");Q18=makeQuery(id+"F31.imprint","IMPRINT",FACE,{"disambiguationData":[TD([[makeQuery(id+"F31.imprint","IMPRINT",EDGE,{"derivedFrom":subQ0}),-1.0]])]});}
            var Q19;
            {var subQ0=sQuery(id+"F31.wireOp",EDGE,"E79.12.0");Q19=makeQuery(id+"F31.imprint","IMPRINT",FACE,{"disambiguationData":[TD([[makeQuery(id+"F31.imprint","IMPRINT",EDGE,{"derivedFrom":subQ0}),-1.0]])]});}
            var Q20;
            {var subQ0=sQuery(id+"F31.wireOp",EDGE,"E79.13.0");Q20=makeQuery(id+"F31.imprint","IMPRINT",FACE,{"disambiguationData":[TD([[makeQuery(id+"F31.imprint","IMPRINT",EDGE,{"derivedFrom":subQ0}),-1.0]])]});}
            var Q21;
            {var subQ0=sQuery(id+"F31.wireOp",EDGE,"E79.14.0");Q21=makeQuery(id+"F31.imprint","IMPRINT",FACE,{"disambiguationData":[TD([[makeQuery(id+"F31.imprint","IMPRINT",EDGE,{"derivedFrom":subQ0}),-1.0]])]});}
            var Q22;
            {var subQ0=sQuery(id+"F31.wireOp",EDGE,"E79.15.0");Q22=makeQuery(id+"F31.imprint","IMPRINT",FACE,{"disambiguationData":[TD([[makeQuery(id+"F31.imprint","IMPRINT",EDGE,{"derivedFrom":subQ0}),-1.0]])]});}
            var Q23;
            {var subQ0=sQuery(id+"F31.wireOp",EDGE,"E79.16.0");Q23=makeQuery(id+"F31.imprint","IMPRINT",FACE,{"disambiguationData":[TD([[makeQuery(id+"F31.imprint","IMPRINT",EDGE,{"derivedFrom":subQ0}),-1.0]])]});}
            var Q24;
            {var subQ0=sQuery(id+"F31.wireOp",EDGE,"E79.17.0");Q24=makeQuery(id+"F31.imprint","IMPRINT",FACE,{"disambiguationData":[TD([[makeQuery(id+"F31.imprint","IMPRINT",EDGE,{"derivedFrom":subQ0}),-1.0]])]});}
            var Q25;
            {var subQ0=sQuery(id+"F31.wireOp",EDGE,"E79.18.0");Q25=makeQuery(id+"F31.imprint","IMPRINT",FACE,{"disambiguationData":[TD([[makeQuery(id+"F31.imprint","IMPRINT",EDGE,{"derivedFrom":subQ0}),-1.0]])]});}
            var Q26;
            {var subQ0=sQuery(id+"F31.wireOp",EDGE,"E79.19.0");Q26=makeQuery(id+"F31.imprint","IMPRINT",FACE,{"disambiguationData":[TD([[makeQuery(id+"F31.imprint","IMPRINT",EDGE,{"derivedFrom":subQ0}),-1.0]])]});}
            var Q27;
            {var subQ0=sQuery(id+"F31.wireOp",EDGE,"E79.20.0");Q27=makeQuery(id+"F31.imprint","IMPRINT",FACE,{"disambiguationData":[TD([[makeQuery(id+"F31.imprint","IMPRINT",EDGE,{"derivedFrom":subQ0}),-1.0]])]});}
            var Q28;
            {var subQ0=sQuery(id+"F31.wireOp",EDGE,"E79.21.0");Q28=makeQuery(id+"F31.imprint","IMPRINT",FACE,{"disambiguationData":[TD([[makeQuery(id+"F31.imprint","IMPRINT",EDGE,{"derivedFrom":subQ0}),-1.0]])]});}
            var Q29;
            {var subQ0=sQuery(id+"F31.wireOp",EDGE,"E79.22.0");Q29=makeQuery(id+"F31.imprint","IMPRINT",FACE,{"disambiguationData":[TD([[makeQuery(id+"F31.imprint","IMPRINT",EDGE,{"derivedFrom":subQ0}),-1.0]])]});}
            var Q30;
            {var subQ0=sQuery(id+"F31.wireOp",EDGE,"E79.23.0");Q30=makeQuery(id+"F31.imprint","IMPRINT",FACE,{"disambiguationData":[TD([[makeQuery(id+"F31.imprint","IMPRINT",EDGE,{"derivedFrom":subQ0}),-1.0]])]});}
            var Q31;
            {var subQ0=sQuery(id+"F31.wireOp",EDGE,"E79.24.0");Q31=makeQuery(id+"F31.imprint","IMPRINT",FACE,{"disambiguationData":[TD([[makeQuery(id+"F31.imprint","IMPRINT",EDGE,{"derivedFrom":subQ0}),-1.0]])]});}
            var Q32;
            {var subQ0=sQuery(id+"F31.wireOp",EDGE,"E79.28.0");Q32=makeQuery(id+"F31.imprint","IMPRINT",FACE,{"disambiguationData":[TD([[makeQuery(id+"F31.imprint","IMPRINT",EDGE,{"derivedFrom":subQ0}),-1.0]])]});}
            var Q33;
            {var subQ0=sQuery(id+"F31.wireOp",EDGE,"E79.25.0");Q33=makeQuery(id+"F31.imprint","IMPRINT",FACE,{"disambiguationData":[TD([[makeQuery(id+"F31.imprint","IMPRINT",EDGE,{"derivedFrom":subQ0}),-1.0]])]});}
            var Q34;
            {var subQ0=sQuery(id+"F31.wireOp",EDGE,"E79.27.0");Q34=makeQuery(id+"F31.imprint","IMPRINT",FACE,{"disambiguationData":[TD([[makeQuery(id+"F31.imprint","IMPRINT",EDGE,{"derivedFrom":subQ0}),-1.0]])]});}
            var Q35;
            {var subQ0=sQuery(id+"F31.wireOp",EDGE,"E79.26.0");Q35=makeQuery(id+"F31.imprint","IMPRINT",FACE,{"disambiguationData":[TD([[makeQuery(id+"F31.imprint","IMPRINT",EDGE,{"derivedFrom":subQ0}),-1.0]])]});}
            extrude(context, id + "F32", {"entities" : qUnion([Q0, Q1, Q2, Q3, Q4, Q5, Q6, Q7, Q8, Q9, Q10, Q11, Q12, Q13, Q14, Q15, Q16, Q17, Q18, Q19, Q20, Q21, Q22, Q23, Q24, Q25, Q26, Q27, Q28, Q29, Q30, Q31, Q32, Q33, Q34, Q35]), "operationType" : NewBodyOperationType.REMOVE, "oppositeDirection" : true, "depth" : 2.5 * mm});
        }
        {
            var Q0;
            Q0=makeQuery(id+"F20.imprint","IMPRINT",FACE,{"disambiguationData":[TD([[makeQuery(id+"F20.imprint","IMPRINT",EDGE,{"derivedFrom":sQuery(id+"F20.wireOp",EDGE,"E42.bottom")}),-1.0]])]});
            var sketch = newSketch(context, id + "F33", { "sketchPlane" : qUnion([Q0])});
            skCircle(sketch, "E80.0", {"center": v(-1.52, 10.88) * mm, "radius": 0.8 * mm, "construction": true});
            skArc(sketch, "E81", {"start": v(5.45, 14.27) * mm, "mid": v(-6.64, 16.7) * mm, "end": v(-5.76, 4.4) * mm});
            skPoint(sketch, "E82.0", {"position": v(7.38, 12.15) * mm});
            skArc(sketch, "E83", {"start": v(6.12, 9.56) * mm, "mid": v(10.23, 12.55) * mm, "end": v(5.45, 14.27) * mm});
            skArc(sketch, "E84", {"start": v(-5.76, 4.4) * mm, "mid": v(1, -7.18) * mm, "end": v(4.34, 5.81) * mm});
            skArc(sketch, "E85.trimOffspring", {"start": v(4.34, 5.81) * mm, "mid": v(5.48, 7.57) * mm, "end": v(6.12, 9.56) * mm});
            skArc(sketch, "E86.0", {"start": v(-9.55, 3.73) * mm, "mid": v(1.48, -10.14) * mm, "end": v(8.08, 6.31) * mm});
            skArc(sketch, "E86.1", {"start": v(6.57, 17.96) * mm, "mid": v(-8.64, 18.94) * mm, "end": v(-9.55, 3.73) * mm});
            skArc(sketch, "E86.2", {"start": v(8.08, 6.31) * mm, "mid": v(13.2, 12.9) * mm, "end": v(6.57, 17.96) * mm});
            skSolve(sketch);
        }
        {
            var Q0;
            Q0=makeQuery(id+"F33.imprint","IMPRINT",FACE,{"disambiguationData":[TD([[makeQuery(id+"F33.imprint","IMPRINT",EDGE,{"derivedFrom":sQuery(id+"F33.wireOp",EDGE,"E81")}),-1.0]])]});
            extrude(context, id + "F34", {"entities" : qUnion([Q0]), "operationType" : NewBodyOperationType.ADD, "depth" : 3 * mm});
        }
        {
            var Q0;
            Q0=makeQuery(id+"F20.imprint","IMPRINT",FACE,{"disambiguationData":[TD([[makeQuery(id+"F20.imprint","IMPRINT",EDGE,{"derivedFrom":sQuery(id+"F20.wireOp",EDGE,"E42.bottom")}),-1.0]])]});
            var sketch = newSketch(context, id + "F35", { "sketchPlane" : qUnion([Q0])});
            skPoint(sketch, "E87.0", {"position": v(-1.53, 10.9) * mm});
            skCircle(sketch, "E88", {"center": v(-1.53, 10.9) * mm, "radius": 3 * mm});
            skCircle(sketch, "E89", {"center": v(-1.53, 10.9) * mm, "radius": 0.8 * mm});
            skSolve(sketch);
        }
        {
            var Q0;
            Q0 = qSketchRegion(id + "F35", true);
            var Q1;
            Q1=makeQuery(id+"F29.boolean.opBoolean","COPY",FACE,{"derivedFrom":makeQuery(id+"F29.opExtrude","CAP_FACE",FACE,{"disambiguationData":[OSD([sQuery(id+"F26.wireOp",EDGE,"E72.0"),sQuery(id+"F28.wireOp",EDGE,"E73")])],"isStart":false})});
            extrude(context, id + "F36", {"entities" : qUnion([Q0]), "operationType" : NewBodyOperationType.ADD, "endBound" : BoundingType.UP_TO_SURFACE, "endBoundEntityFace" : qUnion([Q1]), "depth" : 1 * mm});
        }
        {
            var Q0;
            {var subQ3=sQuery(id+"F20.wireOp",EDGE,"E52.0");var subQ4=makeQuery(id+"F21.opExtrude","SWEPT_FACE",FACE,{"disambiguationData":[OSD([subQ3])]});Q0=makeQuery(id+"F36.boolean.opBoolean","SPLIT",FACE,{"disambiguationData":[TD([subQ4])],"derivedFrom":makeQuery(id+"F34.boolean.opBoolean","SPLIT",FACE,{"disambiguationData":[TD([subQ4])],"derivedFrom":makeQuery(id+"F21.opExtrude","CAP_FACE",FACE,{"disambiguationData":[OSD([sQuery(id+"F20.wireOp",EDGE,"E42.bottom"),sQuery(id+"F20.wireOp",EDGE,"E42.top"),sQuery(id+"F20.wireOp",EDGE,"E42.left"),sQuery(id+"F20.wireOp",EDGE,"E42.right"),subQ3])],"isStart":true})})});}
            var sketch = newSketch(context, id + "F37", { "sketchPlane" : qUnion([Q0])});
            skLineSegment(sketch, "E90", {"start": v(4.04, 3.8) * mm, "end": v(5.28, 4.97) * mm});
            skLineSegment(sketch, "E91", {"start": v(3.32, 4.44) * mm, "end": v(4.34, 5.81) * mm});
            skArc(sketch, "E92", {"start": v(-4.4, 3.36) * mm, "mid": v(-4.68, 2.97) * mm, "end": v(-4.93, 2.55) * mm});
            skLineSegment(sketch, "E93", {"start": v(-4.4, 3.36) * mm, "end": v(-5.76, 4.4) * mm});
            skLineSegment(sketch, "E94", {"start": v(-4.93, 2.55) * mm, "end": v(-6.44, 3.33) * mm});
            skArc(sketch, "E95", {"start": v(-5.76, 4.4) * mm, "mid": v(1, -7.18) * mm, "end": v(4.34, 5.81) * mm});
            skArc(sketch, "E96.trimOffspring", {"start": v(4.04, 3.8) * mm, "mid": v(3.7, 4.14) * mm, "end": v(3.32, 4.44) * mm});
            skSolve(sketch);
        }
        {
            var Q0;
            Q0 = qSketchRegion(id + "F37", true);
            var Q1;
            Q1=makeQuery(id+"F34.opExtrude","CAP_FACE",FACE,{"disambiguationData":[OSD([sQuery(id+"F33.wireOp",EDGE,"E81"),sQuery(id+"F33.wireOp",EDGE,"E83"),sQuery(id+"F33.wireOp",EDGE,"E84"),sQuery(id+"F33.wireOp",EDGE,"E85.trimOffspring"),sQuery(id+"F33.wireOp",EDGE,"E86.0"),sQuery(id+"F33.wireOp",EDGE,"E86.1"),sQuery(id+"F33.wireOp",EDGE,"E86.2")])],"isStart":false});
            extrude(context, id + "F38", {"entities" : qUnion([Q0]), "operationType" : NewBodyOperationType.ADD, "endBound" : BoundingType.UP_TO_SURFACE, "endBoundEntityFace" : qUnion([Q1]), "depth" : 25 * mm});
        }
        {
            var Q0;
            Q0=makeQuery(id+"F27.opExtrude","CAP_FACE",FACE,{"disambiguationData":[OSD([sQuery(id+"F26.wireOp",EDGE,"E71"),sQuery(id+"F26.wireOp",EDGE,"E72.0")])],"isStart":false});
            var sketch = newSketch(context, id + "F39", { "sketchPlane" : qUnion([Q0])});
            skPoint(sketch, "E97.0", {"position": v(7.38, -12.15) * mm});
            skLineSegment(sketch, "E98", {"start": v(7.38, -12.15) * mm, "end": v(5.03, -11.3) * mm, "construction": true});
            skLineSegment(sketch, "E99", {"start": v(7.38, -12.15) * mm, "end": v(4.88, -12.06) * mm, "construction": true});
            skLineSegment(sketch, "E100.MirrorCS", {"start": v(7.38, -12.15) * mm, "end": v(5.41, -10.6) * mm, "construction": true});
            skLineSegment(sketch, "E101", {"start": v(5.88, -11.6) * mm, "end": v(4.88, -12.06) * mm});
            skLineSegment(sketch, "E102", {"start": v(5.41, -10.6) * mm, "end": v(5.88, -11.6) * mm});
            skLineSegment(sketch, "E103.1.0", {"start": v(5.84, -12.59) * mm, "end": v(5.3, -13.54) * mm});
            skLineSegment(sketch, "E103.1.1", {"start": v(4.88, -12.06) * mm, "end": v(5.84, -12.59) * mm});
            skLineSegment(sketch, "E103.2.0", {"start": v(6.4, -13.4) * mm, "end": v(6.53, -14.5) * mm});
            skLineSegment(sketch, "E103.2.1", {"start": v(5.3, -13.54) * mm, "end": v(6.4, -13.4) * mm});
            skLineSegment(sketch, "E103.3.0", {"start": v(7.33, -13.74) * mm, "end": v(8.07, -14.55) * mm});
            skLineSegment(sketch, "E103.3.1", {"start": v(6.53, -14.5) * mm, "end": v(7.33, -13.74) * mm});
            skLineSegment(sketch, "E103.4.0", {"start": v(8.28, -13.47) * mm, "end": v(9.35, -13.68) * mm});
            skLineSegment(sketch, "E103.4.1", {"start": v(8.07, -14.55) * mm, "end": v(8.28, -13.47) * mm});
            skLineSegment(sketch, "E103.5.0", {"start": v(8.89, -12.7) * mm, "end": v(9.88, -12.23) * mm});
            skLineSegment(sketch, "E103.5.1", {"start": v(9.35, -13.68) * mm, "end": v(8.89, -12.7) * mm});
            skLineSegment(sketch, "E103.6.0", {"start": v(8.92, -11.7) * mm, "end": v(9.45, -10.75) * mm});
            skLineSegment(sketch, "E103.6.1", {"start": v(9.88, -12.23) * mm, "end": v(8.92, -11.7) * mm});
            skLineSegment(sketch, "E103.7.0", {"start": v(8.37, -10.88) * mm, "end": v(8.24, -9.8) * mm});
            skLineSegment(sketch, "E103.7.1", {"start": v(9.45, -10.75) * mm, "end": v(8.37, -10.88) * mm});
            skLineSegment(sketch, "E103.8.0", {"start": v(7.44, -10.55) * mm, "end": v(6.7, -9.74) * mm});
            skLineSegment(sketch, "E103.8.1", {"start": v(8.24, -9.8) * mm, "end": v(7.44, -10.55) * mm});
            skLineSegment(sketch, "E103.9.0", {"start": v(6.49, -10.82) * mm, "end": v(5.41, -10.6) * mm});
            skLineSegment(sketch, "E103.9.1", {"start": v(6.7, -9.74) * mm, "end": v(6.49, -10.82) * mm});
            skCircle(sketch, "E104", {"center": v(7.38, -12.15) * mm, "radius": 0.8 * mm});
            skSolve(sketch);
        }
        {
            var Q0;
            Q0 = qSketchRegion(id + "F39", true);
            extrude(context, id + "F40", {"entities" : qUnion([Q0]), "oppositeDirection" : true, "depth" : 4.7 * mm});
        }
        {
            var Q0;
            Q0=makeQuery(id+"F40.opExtrude","CAP_FACE",FACE,{"disambiguationData":[OSD([sQuery(id+"F39.wireOp",EDGE,"E101"),sQuery(id+"F39.wireOp",EDGE,"E102"),sQuery(id+"F39.wireOp",EDGE,"E103.1.0"),sQuery(id+"F39.wireOp",EDGE,"E103.1.1"),sQuery(id+"F39.wireOp",EDGE,"E103.2.0"),sQuery(id+"F39.wireOp",EDGE,"E103.2.1"),sQuery(id+"F39.wireOp",EDGE,"E103.3.0"),sQuery(id+"F39.wireOp",EDGE,"E103.3.1"),sQuery(id+"F39.wireOp",EDGE,"E103.4.0"),sQuery(id+"F39.wireOp",EDGE,"E103.4.1"),sQuery(id+"F39.wireOp",EDGE,"E103.5.0"),sQuery(id+"F39.wireOp",EDGE,"E103.5.1"),sQuery(id+"F39.wireOp",EDGE,"E103.6.0"),sQuery(id+"F39.wireOp",EDGE,"E103.6.1"),sQuery(id+"F39.wireOp",EDGE,"E103.7.0"),sQuery(id+"F39.wireOp",EDGE,"E103.7.1"),sQuery(id+"F39.wireOp",EDGE,"E103.8.0"),sQuery(id+"F39.wireOp",EDGE,"E103.8.1"),sQuery(id+"F39.wireOp",EDGE,"E103.9.0"),sQuery(id+"F39.wireOp",EDGE,"E103.9.1"),sQuery(id+"F39.wireOp",EDGE,"E104")])],"isStart":false});
            var sketch = newSketch(context, id + "F41", { "sketchPlane" : qUnion([Q0])});
            skCircle(sketch, "E105", {"center": v(7.38, 12.15) * mm, "radius": 5 * mm});
            skCircle(sketch, "E106.0", {"center": v(7.38, 12.15) * mm, "radius": 0.8 * mm});
            skSolve(sketch);
        }
        {
            var Q0;
            Q0 = qSketchRegion(id + "F41", true);
            extrude(context, id + "F42", {"entities" : qUnion([Q0]), "operationType" : NewBodyOperationType.ADD, "depth" : 3.75 * mm});
        }
        {
            var Q0;
            Q0=makeQuery(id+"F42.opExtrude","CAP_FACE",FACE,{"disambiguationData":[OSD([sQuery(id+"F41.wireOp",EDGE,"E105"),sQuery(id+"F41.wireOp",EDGE,"E106.0")])],"isStart":false});
            var sketch = newSketch(context, id + "F43", { "sketchPlane" : qUnion([Q0])});
            skCircle(sketch, "E107", {"center": v(7.38, 12.15) * mm, "radius": 7.75 * mm});
            skCircle(sketch, "E108.0", {"center": v(7.38, 12.15) * mm, "radius": 0.8 * mm});
            skSolve(sketch);
        }
        {
            var Q0;
            Q0=makeQuery(id+"F43.imprint","IMPRINT",FACE,{"disambiguationData":[TD([[makeQuery(id+"F43.imprint","IMPRINT",EDGE,{"derivedFrom":sQuery(id+"F43.wireOp",EDGE,"E107")}),1.0]])]});
            var Q1;
            Q1=makeQuery(id+"F43.imprint","IMPRINT",FACE,{"disambiguationData":[TD([[makeQuery(id+"F43.imprint","IMPRINT",EDGE,{"derivedFrom":sQuery(id+"F43.wireOp",EDGE,"E108.0")}),1.0]])]});
            extrude(context, id + "F44", {"entities" : qUnion([Q0, Q1]), "operationType" : NewBodyOperationType.ADD, "depth" : 1.6 * mm});
        }
        {
            var Q0;
            Q0=makeQuery(id+"F44.opExtrude","CAP_FACE",FACE,{"disambiguationData":[OSD([sQuery(id+"F43.wireOp",EDGE,"E107"),sQuery(id+"F43.wireOp",EDGE,"E108.0")])],"isStart":false});
            var sketch = newSketch(context, id + "F45", { "sketchPlane" : qUnion([Q0])});
            skCircle(sketch, "E109", {"center": v(7.38, 12.15) * mm, "radius": 7.5 * mm});
            skCircle(sketch, "E110.0", {"center": v(7.38, 12.15) * mm, "radius": 7.75 * mm});
            skLineSegment(sketch, "E111", {"start": v(7.38, 12.15) * mm, "end": v(-0.3, 11.07) * mm, "construction": true});
            skLineSegment(sketch, "E112", {"start": v(7.38, 12.15) * mm, "end": v(-0.2, 10.57) * mm, "construction": true});
            skLineSegment(sketch, "E113.MirrorCS", {"start": v(7.38, 12.15) * mm, "end": v(-0.35, 11.57) * mm, "construction": true});
            skLineSegment(sketch, "E114", {"start": v(-0.06, 11.25) * mm, "end": v(-0.33, 11.42) * mm});
            skPoint(sketch, "E115.orphan", {"position": v(-0.06, 11.25) * mm});
            skLineSegment(sketch, "E116.MirrorCS", {"start": v(-0.02, 10.95) * mm, "end": v(-0.24, 10.71) * mm});
            skLineSegment(sketch, "E117.1.0", {"start": v(0.12, 10.29) * mm, "end": v(-0.17, 10.42) * mm});
            skLineSegment(sketch, "E117.1.1", {"start": v(0.2, 10) * mm, "end": v(0.02, 9.73) * mm});
            skLineSegment(sketch, "E117.2.0", {"start": v(0.42, 9.35) * mm, "end": v(0.12, 9.45) * mm});
            skLineSegment(sketch, "E117.2.1", {"start": v(0.54, 9.08) * mm, "end": v(0.4, 8.8) * mm});
            skLineSegment(sketch, "E117.3.0", {"start": v(0.84, 8.47) * mm, "end": v(0.53, 8.52) * mm});
            skLineSegment(sketch, "E117.3.1", {"start": v(1, 8.21) * mm, "end": v(0.9, 7.9) * mm});
            skLineSegment(sketch, "E117.4.0", {"start": v(1.38, 7.65) * mm, "end": v(1.06, 7.66) * mm});
            skLineSegment(sketch, "E117.4.1", {"start": v(1.56, 7.41) * mm, "end": v(1.5, 7.1) * mm});
            skLineSegment(sketch, "E117.5.0", {"start": v(2.02, 6.9) * mm, "end": v(1.7, 6.87) * mm});
            skLineSegment(sketch, "E117.5.1", {"start": v(2.23, 6.7) * mm, "end": v(2.2, 6.37) * mm});
            skLineSegment(sketch, "E117.6.0", {"start": v(2.75, 6.25) * mm, "end": v(2.44, 6.18) * mm});
            skLineSegment(sketch, "E117.6.1", {"start": v(2.99, 6.07) * mm, "end": v(3, 5.75) * mm});
            skLineSegment(sketch, "E117.7.0", {"start": v(3.56, 5.7) * mm, "end": v(3.26, 5.58) * mm});
            skLineSegment(sketch, "E117.7.1", {"start": v(3.82, 5.55) * mm, "end": v(3.88, 5.23) * mm});
            skLineSegment(sketch, "E117.8.0", {"start": v(4.43, 5.25) * mm, "end": v(4.15, 5.1) * mm});
            skLineSegment(sketch, "E117.8.1", {"start": v(4.71, 5.14) * mm, "end": v(4.81, 4.83) * mm});
            skLineSegment(sketch, "E117.9.0", {"start": v(5.36, 4.92) * mm, "end": v(5.1, 4.74) * mm});
            skLineSegment(sketch, "E117.9.1", {"start": v(5.65, 4.85) * mm, "end": v(5.79, 4.56) * mm});
            skLineSegment(sketch, "E117.10.0", {"start": v(6.32, 4.72) * mm, "end": v(6.08, 4.5) * mm});
            skLineSegment(sketch, "E117.10.1", {"start": v(6.62, 4.68) * mm, "end": v(6.8, 4.42) * mm});
            skLineSegment(sketch, "E117.11.0", {"start": v(7.3, 4.65) * mm, "end": v(7.1, 4.4) * mm});
            skLineSegment(sketch, "E117.11.1", {"start": v(7.6, 4.65) * mm, "end": v(7.8, 4.4) * mm});
            skLineSegment(sketch, "E117.12.0", {"start": v(8.28, 4.7) * mm, "end": v(8.1, 4.43) * mm});
            skLineSegment(sketch, "E117.12.1", {"start": v(8.57, 4.74) * mm, "end": v(8.81, 4.53) * mm});
            skLineSegment(sketch, "E117.13.0", {"start": v(9.24, 4.88) * mm, "end": v(9.1, 4.59) * mm});
            skLineSegment(sketch, "E117.13.1", {"start": v(9.53, 4.96) * mm, "end": v(9.8, 4.78) * mm});
            skLineSegment(sketch, "E117.14.0", {"start": v(10.17, 5.18) * mm, "end": v(10.08, 4.88) * mm});
            skLineSegment(sketch, "E117.14.1", {"start": v(10.45, 5.3) * mm, "end": v(10.73, 5.16) * mm});
            skLineSegment(sketch, "E117.15.0", {"start": v(11.06, 5.6) * mm, "end": v(11, 5.3) * mm});
            skLineSegment(sketch, "E117.15.1", {"start": v(11.32, 5.76) * mm, "end": v(11.62, 5.66) * mm});
            skLineSegment(sketch, "E117.16.0", {"start": v(11.88, 6.14) * mm, "end": v(11.87, 5.83) * mm});
            skLineSegment(sketch, "E117.16.1", {"start": v(12.12, 6.33) * mm, "end": v(12.43, 6.26) * mm});
            skLineSegment(sketch, "E117.17.0", {"start": v(12.62, 6.78) * mm, "end": v(12.65, 6.46) * mm});
            skLineSegment(sketch, "E117.17.1", {"start": v(12.83, 7) * mm, "end": v(13.15, 6.97) * mm});
            skLineSegment(sketch, "E117.18.0", {"start": v(13.28, 7.51) * mm, "end": v(13.35, 7.2) * mm});
            skLineSegment(sketch, "E117.18.1", {"start": v(13.46, 7.75) * mm, "end": v(13.78, 7.77) * mm});
            skLineSegment(sketch, "E117.19.0", {"start": v(13.83, 8.32) * mm, "end": v(13.94, 8.02) * mm});
            skLineSegment(sketch, "E117.19.1", {"start": v(13.98, 8.58) * mm, "end": v(14.3, 8.64) * mm});
            skLineSegment(sketch, "E117.20.0", {"start": v(14.28, 9.2) * mm, "end": v(14.43, 8.91) * mm});
            skLineSegment(sketch, "E117.20.1", {"start": v(14.4, 9.48) * mm, "end": v(14.7, 9.58) * mm});
            skLineSegment(sketch, "E117.21.0", {"start": v(14.6, 10.12) * mm, "end": v(14.79, 9.86) * mm});
            skLineSegment(sketch, "E117.21.1", {"start": v(14.68, 10.41) * mm, "end": v(14.97, 10.55) * mm});
            skLineSegment(sketch, "E117.22.0", {"start": v(14.8, 11.08) * mm, "end": v(15.02, 10.85) * mm});
            skLineSegment(sketch, "E117.22.1", {"start": v(14.84, 11.38) * mm, "end": v(15.1, 11.56) * mm});
            skLineSegment(sketch, "E117.23.0", {"start": v(14.88, 12.06) * mm, "end": v(15.13, 11.86) * mm});
            skLineSegment(sketch, "E117.23.1", {"start": v(14.88, 12.36) * mm, "end": v(15.12, 12.57) * mm});
            skLineSegment(sketch, "E117.24.0", {"start": v(14.83, 13.04) * mm, "end": v(15.1, 12.87) * mm});
            skLineSegment(sketch, "E117.24.1", {"start": v(14.79, 13.34) * mm, "end": v(15, 13.58) * mm});
            skLineSegment(sketch, "E117.25.0", {"start": v(14.65, 14) * mm, "end": v(14.94, 13.87) * mm});
            skLineSegment(sketch, "E117.25.1", {"start": v(14.57, 14.3) * mm, "end": v(14.75, 14.56) * mm});
            skLineSegment(sketch, "E117.26.0", {"start": v(14.34, 14.94) * mm, "end": v(14.65, 14.84) * mm});
            skLineSegment(sketch, "E117.26.1", {"start": v(14.23, 15.21) * mm, "end": v(14.37, 15.5) * mm});
            skLineSegment(sketch, "E117.27.0", {"start": v(13.92, 15.82) * mm, "end": v(14.23, 15.77) * mm});
            skLineSegment(sketch, "E117.27.1", {"start": v(13.77, 16.08) * mm, "end": v(13.87, 16.38) * mm});
            skLineSegment(sketch, "E117.28.0", {"start": v(13.38, 16.64) * mm, "end": v(13.7, 16.63) * mm});
            skLineSegment(sketch, "E117.28.1", {"start": v(13.2, 16.88) * mm, "end": v(13.26, 17.2) * mm});
            skLineSegment(sketch, "E117.29.0", {"start": v(12.74, 17.39) * mm, "end": v(13.06, 17.42) * mm});
            skLineSegment(sketch, "E117.29.1", {"start": v(12.53, 17.6) * mm, "end": v(12.55, 17.92) * mm});
            skLineSegment(sketch, "E117.30.0", {"start": v(12.01, 18.04) * mm, "end": v(12.33, 18.11) * mm});
            skLineSegment(sketch, "E117.30.1", {"start": v(11.77, 18.22) * mm, "end": v(11.76, 18.54) * mm});
            skLineSegment(sketch, "E117.31.0", {"start": v(11.2, 18.6) * mm, "end": v(11.5, 18.7) * mm});
            skLineSegment(sketch, "E117.31.1", {"start": v(10.94, 18.75) * mm, "end": v(10.88, 19.06) * mm});
            skLineSegment(sketch, "E117.32.0", {"start": v(10.33, 19.04) * mm, "end": v(10.61, 19.19) * mm});
            skLineSegment(sketch, "E117.32.1", {"start": v(10.05, 19.15) * mm, "end": v(9.95, 19.46) * mm});
            skLineSegment(sketch, "E117.33.0", {"start": v(9.4, 19.37) * mm, "end": v(9.67, 19.55) * mm});
            skLineSegment(sketch, "E117.33.1", {"start": v(9.11, 19.44) * mm, "end": v(8.97, 19.73) * mm});
            skLineSegment(sketch, "E117.34.0", {"start": v(8.44, 19.57) * mm, "end": v(8.68, 19.79) * mm});
            skLineSegment(sketch, "E117.34.1", {"start": v(8.15, 19.6) * mm, "end": v(7.97, 19.87) * mm});
            skLineSegment(sketch, "E117.35.0", {"start": v(7.47, 19.65) * mm, "end": v(7.67, 19.9) * mm});
            skLineSegment(sketch, "E117.35.1", {"start": v(7.17, 19.64) * mm, "end": v(6.96, 19.88) * mm});
            skLineSegment(sketch, "E117.36.0", {"start": v(6.49, 19.6) * mm, "end": v(6.66, 19.86) * mm});
            skLineSegment(sketch, "E117.36.1", {"start": v(6.19, 19.55) * mm, "end": v(5.95, 19.76) * mm});
            skLineSegment(sketch, "E117.37.0", {"start": v(5.52, 19.41) * mm, "end": v(5.66, 19.7) * mm});
            skLineSegment(sketch, "E117.37.1", {"start": v(5.23, 19.33) * mm, "end": v(4.97, 19.51) * mm});
            skLineSegment(sketch, "E117.38.0", {"start": v(4.59, 19.1) * mm, "end": v(4.68, 19.41) * mm});
            skLineSegment(sketch, "E117.38.1", {"start": v(4.31, 18.99) * mm, "end": v(4.03, 19.13) * mm});
            skLineSegment(sketch, "E117.39.0", {"start": v(3.7, 18.68) * mm, "end": v(3.76, 19) * mm});
            skLineSegment(sketch, "E117.39.1", {"start": v(3.45, 18.53) * mm, "end": v(3.15, 18.64) * mm});
            skLineSegment(sketch, "E117.40.0", {"start": v(2.88, 18.15) * mm, "end": v(2.9, 18.47) * mm});
            skLineSegment(sketch, "E117.40.1", {"start": v(2.65, 17.96) * mm, "end": v(2.33, 18.03) * mm});
            skLineSegment(sketch, "E117.41.0", {"start": v(2.14, 17.5) * mm, "end": v(2.1, 17.83) * mm});
            skLineSegment(sketch, "E117.41.1", {"start": v(1.93, 17.3) * mm, "end": v(1.6, 17.32) * mm});
            skLineSegment(sketch, "E117.42.0", {"start": v(1.48, 16.78) * mm, "end": v(1.41, 17.09) * mm});
            skLineSegment(sketch, "E117.42.1", {"start": v(1.3, 16.54) * mm, "end": v(0.98, 16.52) * mm});
            skLineSegment(sketch, "E117.43.0", {"start": v(0.93, 15.97) * mm, "end": v(0.82, 16.27) * mm});
            skLineSegment(sketch, "E117.43.1", {"start": v(0.78, 15.7) * mm, "end": v(0.47, 15.65) * mm});
            skLineSegment(sketch, "E117.44.0", {"start": v(0.49, 15.1) * mm, "end": v(0.34, 15.38) * mm});
            skLineSegment(sketch, "E117.44.1", {"start": v(0.37, 14.82) * mm, "end": v(0.07, 14.72) * mm});
            skLineSegment(sketch, "E117.45.0", {"start": v(0.16, 14.17) * mm, "end": v(-0.02, 14.43) * mm});
            skLineSegment(sketch, "E117.45.1", {"start": v(0.08, 13.88) * mm, "end": v(-0.2, 13.74) * mm});
            skLineSegment(sketch, "E117.46.0", {"start": v(-0.04, 13.2) * mm, "end": v(-0.26, 13.44) * mm});
            skLineSegment(sketch, "E117.46.1", {"start": v(-0.08, 12.91) * mm, "end": v(-0.35, 12.74) * mm});
            skLineSegment(sketch, "E117.47.0", {"start": v(-0.12, 12.23) * mm, "end": v(-0.36, 12.43) * mm});
            skLineSegment(sketch, "E117.47.1", {"start": v(-0.12, 11.93) * mm, "end": v(-0.36, 11.72) * mm});
            skSolve(sketch);
        }
        {
            var Q0;
            {var subQ0=sQuery(id+"F45.wireOp",EDGE,"c415bd7c-024f-4278-887f-026b6ff02143.26.0");Q0=makeQuery(id+"F45.imprint","IMPRINT",FACE,{"disambiguationData":[TD([[makeQuery(id+"F45.imprint","IMPRINT",EDGE,{"derivedFrom":subQ0}),1.0]])]});}
            var Q1;
            {var subQ0=sQuery(id+"F45.wireOp",EDGE,"c415bd7c-024f-4278-887f-026b6ff02143.27.0");Q1=makeQuery(id+"F45.imprint","IMPRINT",FACE,{"disambiguationData":[TD([[makeQuery(id+"F45.imprint","IMPRINT",EDGE,{"derivedFrom":subQ0}),1.0]])]});}
            var Q2;
            {var subQ0=sQuery(id+"F45.wireOp",EDGE,"c415bd7c-024f-4278-887f-026b6ff02143.28.0");Q2=makeQuery(id+"F45.imprint","IMPRINT",FACE,{"disambiguationData":[TD([[makeQuery(id+"F45.imprint","IMPRINT",EDGE,{"derivedFrom":subQ0}),1.0]])]});}
            var Q3;
            {var subQ0=sQuery(id+"F45.wireOp",EDGE,"c415bd7c-024f-4278-887f-026b6ff02143.29.0");Q3=makeQuery(id+"F45.imprint","IMPRINT",FACE,{"disambiguationData":[TD([[makeQuery(id+"F45.imprint","IMPRINT",EDGE,{"derivedFrom":subQ0}),1.0]])]});}
            var Q4;
            {var subQ0=sQuery(id+"F45.wireOp",EDGE,"c415bd7c-024f-4278-887f-026b6ff02143.30.0");Q4=makeQuery(id+"F45.imprint","IMPRINT",FACE,{"disambiguationData":[TD([[makeQuery(id+"F45.imprint","IMPRINT",EDGE,{"derivedFrom":subQ0}),1.0]])]});}
            var Q5;
            {var subQ0=sQuery(id+"F45.wireOp",EDGE,"c415bd7c-024f-4278-887f-026b6ff02143.31.0");Q5=makeQuery(id+"F45.imprint","IMPRINT",FACE,{"disambiguationData":[TD([[makeQuery(id+"F45.imprint","IMPRINT",EDGE,{"derivedFrom":subQ0}),1.0]])]});}
            var Q6;
            {var subQ0=sQuery(id+"F45.wireOp",EDGE,"c415bd7c-024f-4278-887f-026b6ff02143.32.0");Q6=makeQuery(id+"F45.imprint","IMPRINT",FACE,{"disambiguationData":[TD([[makeQuery(id+"F45.imprint","IMPRINT",EDGE,{"derivedFrom":subQ0}),1.0]])]});}
            var Q7;
            {var subQ0=sQuery(id+"F45.wireOp",EDGE,"c415bd7c-024f-4278-887f-026b6ff02143.33.0");Q7=makeQuery(id+"F45.imprint","IMPRINT",FACE,{"disambiguationData":[TD([[makeQuery(id+"F45.imprint","IMPRINT",EDGE,{"derivedFrom":subQ0}),1.0]])]});}
            var Q8;
            {var subQ0=sQuery(id+"F45.wireOp",EDGE,"c415bd7c-024f-4278-887f-026b6ff02143.34.0");Q8=makeQuery(id+"F45.imprint","IMPRINT",FACE,{"disambiguationData":[TD([[makeQuery(id+"F45.imprint","IMPRINT",EDGE,{"derivedFrom":subQ0}),1.0]])]});}
            var Q9;
            {var subQ0=sQuery(id+"F45.wireOp",EDGE,"c415bd7c-024f-4278-887f-026b6ff02143.35.0");Q9=makeQuery(id+"F45.imprint","IMPRINT",FACE,{"disambiguationData":[TD([[makeQuery(id+"F45.imprint","IMPRINT",EDGE,{"derivedFrom":subQ0}),1.0]])]});}
            var Q10;
            {var subQ0=sQuery(id+"F45.wireOp",EDGE,"c415bd7c-024f-4278-887f-026b6ff02143.36.0");Q10=makeQuery(id+"F45.imprint","IMPRINT",FACE,{"disambiguationData":[TD([[makeQuery(id+"F45.imprint","IMPRINT",EDGE,{"derivedFrom":subQ0}),1.0]])]});}
            var Q11;
            {var subQ0=sQuery(id+"F45.wireOp",EDGE,"c415bd7c-024f-4278-887f-026b6ff02143.37.0");Q11=makeQuery(id+"F45.imprint","IMPRINT",FACE,{"disambiguationData":[TD([[makeQuery(id+"F45.imprint","IMPRINT",EDGE,{"derivedFrom":subQ0}),1.0]])]});}
            var Q12;
            {var subQ0=sQuery(id+"F45.wireOp",EDGE,"c415bd7c-024f-4278-887f-026b6ff02143.38.0");Q12=makeQuery(id+"F45.imprint","IMPRINT",FACE,{"disambiguationData":[TD([[makeQuery(id+"F45.imprint","IMPRINT",EDGE,{"derivedFrom":subQ0}),1.0]])]});}
            var Q13;
            {var subQ0=sQuery(id+"F45.wireOp",EDGE,"c415bd7c-024f-4278-887f-026b6ff02143.39.0");Q13=makeQuery(id+"F45.imprint","IMPRINT",FACE,{"disambiguationData":[TD([[makeQuery(id+"F45.imprint","IMPRINT",EDGE,{"derivedFrom":subQ0}),1.0]])]});}
            var Q14;
            {var subQ0=sQuery(id+"F45.wireOp",EDGE,"c415bd7c-024f-4278-887f-026b6ff02143.40.0");Q14=makeQuery(id+"F45.imprint","IMPRINT",FACE,{"disambiguationData":[TD([[makeQuery(id+"F45.imprint","IMPRINT",EDGE,{"derivedFrom":subQ0}),1.0]])]});}
            var Q15;
            {var subQ0=sQuery(id+"F45.wireOp",EDGE,"c415bd7c-024f-4278-887f-026b6ff02143.41.0");Q15=makeQuery(id+"F45.imprint","IMPRINT",FACE,{"disambiguationData":[TD([[makeQuery(id+"F45.imprint","IMPRINT",EDGE,{"derivedFrom":subQ0}),1.0]])]});}
            var Q16;
            {var subQ0=sQuery(id+"F45.wireOp",EDGE,"c415bd7c-024f-4278-887f-026b6ff02143.42.0");Q16=makeQuery(id+"F45.imprint","IMPRINT",FACE,{"disambiguationData":[TD([[makeQuery(id+"F45.imprint","IMPRINT",EDGE,{"derivedFrom":subQ0}),1.0]])]});}
            var Q17;
            {var subQ0=sQuery(id+"F45.wireOp",EDGE,"c415bd7c-024f-4278-887f-026b6ff02143.43.0");Q17=makeQuery(id+"F45.imprint","IMPRINT",FACE,{"disambiguationData":[TD([[makeQuery(id+"F45.imprint","IMPRINT",EDGE,{"derivedFrom":subQ0}),1.0]])]});}
            var Q18;
            {var subQ0=sQuery(id+"F45.wireOp",EDGE,"c415bd7c-024f-4278-887f-026b6ff02143.44.0");Q18=makeQuery(id+"F45.imprint","IMPRINT",FACE,{"disambiguationData":[TD([[makeQuery(id+"F45.imprint","IMPRINT",EDGE,{"derivedFrom":subQ0}),1.0]])]});}
            var Q19;
            {var subQ0=sQuery(id+"F45.wireOp",EDGE,"c415bd7c-024f-4278-887f-026b6ff02143.45.0");Q19=makeQuery(id+"F45.imprint","IMPRINT",FACE,{"disambiguationData":[TD([[makeQuery(id+"F45.imprint","IMPRINT",EDGE,{"derivedFrom":subQ0}),1.0]])]});}
            var Q20;
            {var subQ0=sQuery(id+"F45.wireOp",EDGE,"c415bd7c-024f-4278-887f-026b6ff02143.46.0");Q20=makeQuery(id+"F45.imprint","IMPRINT",FACE,{"disambiguationData":[TD([[makeQuery(id+"F45.imprint","IMPRINT",EDGE,{"derivedFrom":subQ0}),1.0]])]});}
            var Q21;
            {var subQ0=sQuery(id+"F45.wireOp",EDGE,"c415bd7c-024f-4278-887f-026b6ff02143.47.0");Q21=makeQuery(id+"F45.imprint","IMPRINT",FACE,{"disambiguationData":[TD([[makeQuery(id+"F45.imprint","IMPRINT",EDGE,{"derivedFrom":subQ0}),1.0]])]});}
            var Q22;
            Q22=makeQuery(id+"F45.imprint","IMPRINT",FACE,{"disambiguationData":[TD([[makeQuery(id+"F45.imprint","IMPRINT",EDGE,{"derivedFrom":makeQuery(id+"F44.opExtrude","CAP_EDGE",EDGE,{"disambiguationData":[OSD([sQuery(id+"F43.wireOp",EDGE,"E108.0")])],"isStart":false})}),-1.0]])]});
            var Q23;
            {var subQ0=sQuery(id+"F45.wireOp",EDGE,"E117.37.0");Q23=makeQuery(id+"F45.imprint","IMPRINT",FACE,{"disambiguationData":[TD([[makeQuery(id+"F45.imprint","IMPRINT",EDGE,{"derivedFrom":subQ0}),1.0]])]});}
            var Q24;
            {var subQ0=sQuery(id+"F45.wireOp",EDGE,"E117.36.0");Q24=makeQuery(id+"F45.imprint","IMPRINT",FACE,{"disambiguationData":[TD([[makeQuery(id+"F45.imprint","IMPRINT",EDGE,{"derivedFrom":subQ0}),1.0]])]});}
            var Q25;
            {var subQ0=sQuery(id+"F45.wireOp",EDGE,"E117.35.0");Q25=makeQuery(id+"F45.imprint","IMPRINT",FACE,{"disambiguationData":[TD([[makeQuery(id+"F45.imprint","IMPRINT",EDGE,{"derivedFrom":subQ0}),1.0]])]});}
            var Q26;
            {var subQ0=sQuery(id+"F45.wireOp",EDGE,"E117.34.0");Q26=makeQuery(id+"F45.imprint","IMPRINT",FACE,{"disambiguationData":[TD([[makeQuery(id+"F45.imprint","IMPRINT",EDGE,{"derivedFrom":subQ0}),1.0]])]});}
            var Q27;
            {var subQ0=sQuery(id+"F45.wireOp",EDGE,"E117.33.0");Q27=makeQuery(id+"F45.imprint","IMPRINT",FACE,{"disambiguationData":[TD([[makeQuery(id+"F45.imprint","IMPRINT",EDGE,{"derivedFrom":subQ0}),1.0]])]});}
            var Q28;
            {var subQ0=sQuery(id+"F45.wireOp",EDGE,"E117.32.0");Q28=makeQuery(id+"F45.imprint","IMPRINT",FACE,{"disambiguationData":[TD([[makeQuery(id+"F45.imprint","IMPRINT",EDGE,{"derivedFrom":subQ0}),1.0]])]});}
            var Q29;
            {var subQ0=sQuery(id+"F45.wireOp",EDGE,"E117.31.0");Q29=makeQuery(id+"F45.imprint","IMPRINT",FACE,{"disambiguationData":[TD([[makeQuery(id+"F45.imprint","IMPRINT",EDGE,{"derivedFrom":subQ0}),1.0]])]});}
            var Q30;
            {var subQ0=sQuery(id+"F45.wireOp",EDGE,"E117.30.0");Q30=makeQuery(id+"F45.imprint","IMPRINT",FACE,{"disambiguationData":[TD([[makeQuery(id+"F45.imprint","IMPRINT",EDGE,{"derivedFrom":subQ0}),1.0]])]});}
            var Q31;
            {var subQ0=sQuery(id+"F45.wireOp",EDGE,"E117.29.0");Q31=makeQuery(id+"F45.imprint","IMPRINT",FACE,{"disambiguationData":[TD([[makeQuery(id+"F45.imprint","IMPRINT",EDGE,{"derivedFrom":subQ0}),1.0]])]});}
            var Q32;
            {var subQ0=sQuery(id+"F45.wireOp",EDGE,"E117.28.0");Q32=makeQuery(id+"F45.imprint","IMPRINT",FACE,{"disambiguationData":[TD([[makeQuery(id+"F45.imprint","IMPRINT",EDGE,{"derivedFrom":subQ0}),1.0]])]});}
            var Q33;
            {var subQ0=sQuery(id+"F45.wireOp",EDGE,"E117.27.0");Q33=makeQuery(id+"F45.imprint","IMPRINT",FACE,{"disambiguationData":[TD([[makeQuery(id+"F45.imprint","IMPRINT",EDGE,{"derivedFrom":subQ0}),1.0]])]});}
            var Q34;
            {var subQ0=sQuery(id+"F45.wireOp",EDGE,"E117.26.0");Q34=makeQuery(id+"F45.imprint","IMPRINT",FACE,{"disambiguationData":[TD([[makeQuery(id+"F45.imprint","IMPRINT",EDGE,{"derivedFrom":subQ0}),1.0]])]});}
            var Q35;
            {var subQ0=sQuery(id+"F45.wireOp",EDGE,"E117.25.0");Q35=makeQuery(id+"F45.imprint","IMPRINT",FACE,{"disambiguationData":[TD([[makeQuery(id+"F45.imprint","IMPRINT",EDGE,{"derivedFrom":subQ0}),1.0]])]});}
            var Q36;
            {var subQ0=sQuery(id+"F45.wireOp",EDGE,"E117.24.0");Q36=makeQuery(id+"F45.imprint","IMPRINT",FACE,{"disambiguationData":[TD([[makeQuery(id+"F45.imprint","IMPRINT",EDGE,{"derivedFrom":subQ0}),1.0]])]});}
            var Q37;
            {var subQ0=sQuery(id+"F45.wireOp",EDGE,"E117.23.0");Q37=makeQuery(id+"F45.imprint","IMPRINT",FACE,{"disambiguationData":[TD([[makeQuery(id+"F45.imprint","IMPRINT",EDGE,{"derivedFrom":subQ0}),1.0]])]});}
            var Q38;
            {var subQ0=sQuery(id+"F45.wireOp",EDGE,"E117.22.0");Q38=makeQuery(id+"F45.imprint","IMPRINT",FACE,{"disambiguationData":[TD([[makeQuery(id+"F45.imprint","IMPRINT",EDGE,{"derivedFrom":subQ0}),1.0]])]});}
            var Q39;
            {var subQ0=sQuery(id+"F45.wireOp",EDGE,"E117.21.0");Q39=makeQuery(id+"F45.imprint","IMPRINT",FACE,{"disambiguationData":[TD([[makeQuery(id+"F45.imprint","IMPRINT",EDGE,{"derivedFrom":subQ0}),1.0]])]});}
            var Q40;
            {var subQ0=sQuery(id+"F45.wireOp",EDGE,"E117.20.0");Q40=makeQuery(id+"F45.imprint","IMPRINT",FACE,{"disambiguationData":[TD([[makeQuery(id+"F45.imprint","IMPRINT",EDGE,{"derivedFrom":subQ0}),1.0]])]});}
            var Q41;
            {var subQ0=sQuery(id+"F45.wireOp",EDGE,"E117.19.0");Q41=makeQuery(id+"F45.imprint","IMPRINT",FACE,{"disambiguationData":[TD([[makeQuery(id+"F45.imprint","IMPRINT",EDGE,{"derivedFrom":subQ0}),1.0]])]});}
            var Q42;
            {var subQ0=sQuery(id+"F45.wireOp",EDGE,"E117.18.0");Q42=makeQuery(id+"F45.imprint","IMPRINT",FACE,{"disambiguationData":[TD([[makeQuery(id+"F45.imprint","IMPRINT",EDGE,{"derivedFrom":subQ0}),1.0]])]});}
            var Q43;
            {var subQ0=sQuery(id+"F45.wireOp",EDGE,"E117.17.0");Q43=makeQuery(id+"F45.imprint","IMPRINT",FACE,{"disambiguationData":[TD([[makeQuery(id+"F45.imprint","IMPRINT",EDGE,{"derivedFrom":subQ0}),1.0]])]});}
            var Q44;
            {var subQ0=sQuery(id+"F45.wireOp",EDGE,"E117.16.0");Q44=makeQuery(id+"F45.imprint","IMPRINT",FACE,{"disambiguationData":[TD([[makeQuery(id+"F45.imprint","IMPRINT",EDGE,{"derivedFrom":subQ0}),1.0]])]});}
            var Q45;
            {var subQ0=sQuery(id+"F45.wireOp",EDGE,"E117.15.0");Q45=makeQuery(id+"F45.imprint","IMPRINT",FACE,{"disambiguationData":[TD([[makeQuery(id+"F45.imprint","IMPRINT",EDGE,{"derivedFrom":subQ0}),1.0]])]});}
            var Q46;
            {var subQ0=sQuery(id+"F45.wireOp",EDGE,"E117.14.0");Q46=makeQuery(id+"F45.imprint","IMPRINT",FACE,{"disambiguationData":[TD([[makeQuery(id+"F45.imprint","IMPRINT",EDGE,{"derivedFrom":subQ0}),1.0]])]});}
            var Q47;
            {var subQ0=sQuery(id+"F45.wireOp",EDGE,"E117.13.0");Q47=makeQuery(id+"F45.imprint","IMPRINT",FACE,{"disambiguationData":[TD([[makeQuery(id+"F45.imprint","IMPRINT",EDGE,{"derivedFrom":subQ0}),1.0]])]});}
            var Q48;
            {var subQ0=sQuery(id+"F45.wireOp",EDGE,"E117.12.0");Q48=makeQuery(id+"F45.imprint","IMPRINT",FACE,{"disambiguationData":[TD([[makeQuery(id+"F45.imprint","IMPRINT",EDGE,{"derivedFrom":subQ0}),1.0]])]});}
            var Q49;
            {var subQ0=sQuery(id+"F45.wireOp",EDGE,"E117.11.0");Q49=makeQuery(id+"F45.imprint","IMPRINT",FACE,{"disambiguationData":[TD([[makeQuery(id+"F45.imprint","IMPRINT",EDGE,{"derivedFrom":subQ0}),1.0]])]});}
            var Q50;
            {var subQ0=sQuery(id+"F45.wireOp",EDGE,"E117.10.0");Q50=makeQuery(id+"F45.imprint","IMPRINT",FACE,{"disambiguationData":[TD([[makeQuery(id+"F45.imprint","IMPRINT",EDGE,{"derivedFrom":subQ0}),1.0]])]});}
            var Q51;
            {var subQ0=sQuery(id+"F45.wireOp",EDGE,"E117.9.0");Q51=makeQuery(id+"F45.imprint","IMPRINT",FACE,{"disambiguationData":[TD([[makeQuery(id+"F45.imprint","IMPRINT",EDGE,{"derivedFrom":subQ0}),1.0]])]});}
            var Q52;
            {var subQ0=sQuery(id+"F45.wireOp",EDGE,"E117.8.0");Q52=makeQuery(id+"F45.imprint","IMPRINT",FACE,{"disambiguationData":[TD([[makeQuery(id+"F45.imprint","IMPRINT",EDGE,{"derivedFrom":subQ0}),1.0]])]});}
            var Q53;
            {var subQ0=sQuery(id+"F45.wireOp",EDGE,"E117.7.0");Q53=makeQuery(id+"F45.imprint","IMPRINT",FACE,{"disambiguationData":[TD([[makeQuery(id+"F45.imprint","IMPRINT",EDGE,{"derivedFrom":subQ0}),1.0]])]});}
            var Q54;
            {var subQ0=sQuery(id+"F45.wireOp",EDGE,"E117.6.0");Q54=makeQuery(id+"F45.imprint","IMPRINT",FACE,{"disambiguationData":[TD([[makeQuery(id+"F45.imprint","IMPRINT",EDGE,{"derivedFrom":subQ0}),1.0]])]});}
            var Q55;
            {var subQ0=sQuery(id+"F45.wireOp",EDGE,"E117.5.0");Q55=makeQuery(id+"F45.imprint","IMPRINT",FACE,{"disambiguationData":[TD([[makeQuery(id+"F45.imprint","IMPRINT",EDGE,{"derivedFrom":subQ0}),1.0]])]});}
            var Q56;
            {var subQ0=sQuery(id+"F45.wireOp",EDGE,"E117.4.0");Q56=makeQuery(id+"F45.imprint","IMPRINT",FACE,{"disambiguationData":[TD([[makeQuery(id+"F45.imprint","IMPRINT",EDGE,{"derivedFrom":subQ0}),1.0]])]});}
            var Q57;
            {var subQ0=sQuery(id+"F45.wireOp",EDGE,"E117.3.0");Q57=makeQuery(id+"F45.imprint","IMPRINT",FACE,{"disambiguationData":[TD([[makeQuery(id+"F45.imprint","IMPRINT",EDGE,{"derivedFrom":subQ0}),1.0]])]});}
            var Q58;
            {var subQ0=sQuery(id+"F45.wireOp",EDGE,"E117.2.0");Q58=makeQuery(id+"F45.imprint","IMPRINT",FACE,{"disambiguationData":[TD([[makeQuery(id+"F45.imprint","IMPRINT",EDGE,{"derivedFrom":subQ0}),1.0]])]});}
            var Q59;
            {var subQ0=sQuery(id+"F45.wireOp",EDGE,"E117.38.0");Q59=makeQuery(id+"F45.imprint","IMPRINT",FACE,{"disambiguationData":[TD([[makeQuery(id+"F45.imprint","IMPRINT",EDGE,{"derivedFrom":subQ0}),1.0]])]});}
            var Q60;
            {var subQ0=sQuery(id+"F45.wireOp",EDGE,"E117.39.0");Q60=makeQuery(id+"F45.imprint","IMPRINT",FACE,{"disambiguationData":[TD([[makeQuery(id+"F45.imprint","IMPRINT",EDGE,{"derivedFrom":subQ0}),1.0]])]});}
            var Q61;
            {var subQ0=sQuery(id+"F45.wireOp",EDGE,"E117.40.0");Q61=makeQuery(id+"F45.imprint","IMPRINT",FACE,{"disambiguationData":[TD([[makeQuery(id+"F45.imprint","IMPRINT",EDGE,{"derivedFrom":subQ0}),1.0]])]});}
            var Q62;
            {var subQ0=sQuery(id+"F45.wireOp",EDGE,"E117.41.0");Q62=makeQuery(id+"F45.imprint","IMPRINT",FACE,{"disambiguationData":[TD([[makeQuery(id+"F45.imprint","IMPRINT",EDGE,{"derivedFrom":subQ0}),1.0]])]});}
            var Q63;
            {var subQ0=sQuery(id+"F45.wireOp",EDGE,"E117.42.0");Q63=makeQuery(id+"F45.imprint","IMPRINT",FACE,{"disambiguationData":[TD([[makeQuery(id+"F45.imprint","IMPRINT",EDGE,{"derivedFrom":subQ0}),1.0]])]});}
            var Q64;
            {var subQ0=sQuery(id+"F45.wireOp",EDGE,"E117.43.0");Q64=makeQuery(id+"F45.imprint","IMPRINT",FACE,{"disambiguationData":[TD([[makeQuery(id+"F45.imprint","IMPRINT",EDGE,{"derivedFrom":subQ0}),1.0]])]});}
            var Q65;
            {var subQ0=sQuery(id+"F45.wireOp",EDGE,"E117.44.0");Q65=makeQuery(id+"F45.imprint","IMPRINT",FACE,{"disambiguationData":[TD([[makeQuery(id+"F45.imprint","IMPRINT",EDGE,{"derivedFrom":subQ0}),1.0]])]});}
            var Q66;
            {var subQ0=sQuery(id+"F45.wireOp",EDGE,"E117.45.0");Q66=makeQuery(id+"F45.imprint","IMPRINT",FACE,{"disambiguationData":[TD([[makeQuery(id+"F45.imprint","IMPRINT",EDGE,{"derivedFrom":subQ0}),1.0]])]});}
            var Q67;
            {var subQ0=sQuery(id+"F45.wireOp",EDGE,"E117.46.0");Q67=makeQuery(id+"F45.imprint","IMPRINT",FACE,{"disambiguationData":[TD([[makeQuery(id+"F45.imprint","IMPRINT",EDGE,{"derivedFrom":subQ0}),1.0]])]});}
            var Q68;
            {var subQ0=sQuery(id+"F45.wireOp",EDGE,"E117.47.0");Q68=makeQuery(id+"F45.imprint","IMPRINT",FACE,{"disambiguationData":[TD([[makeQuery(id+"F45.imprint","IMPRINT",EDGE,{"derivedFrom":subQ0}),1.0]])]});}
            var Q69;
            {var subQ0=sQuery(id+"F45.wireOp",EDGE,"E114");Q69=makeQuery(id+"F45.imprint","IMPRINT",FACE,{"disambiguationData":[TD([[makeQuery(id+"F45.imprint","IMPRINT",EDGE,{"derivedFrom":subQ0}),1.0]])]});}
            var Q70;
            {var subQ0=sQuery(id+"F45.wireOp",EDGE,"E117.1.0");Q70=makeQuery(id+"F45.imprint","IMPRINT",FACE,{"disambiguationData":[TD([[makeQuery(id+"F45.imprint","IMPRINT",EDGE,{"derivedFrom":subQ0}),1.0]])]});}
            extrude(context, id + "F46", {"entities" : qUnion([Q0, Q1, Q2, Q3, Q4, Q5, Q6, Q7, Q8, Q9, Q10, Q11, Q12, Q13, Q14, Q15, Q16, Q17, Q18, Q19, Q20, Q21, Q22, Q23, Q24, Q25, Q26, Q27, Q28, Q29, Q30, Q31, Q32, Q33, Q34, Q35, Q36, Q37, Q38, Q39, Q40, Q41, Q42, Q43, Q44, Q45, Q46, Q47, Q48, Q49, Q50, Q51, Q52, Q53, Q54, Q55, Q56, Q57, Q58, Q59, Q60, Q61, Q62, Q63, Q64, Q65, Q66, Q67, Q68, Q69, Q70]), "operationType" : NewBodyOperationType.REMOVE, "endBound" : BoundingType.UP_TO_NEXT, "oppositeDirection" : true, "depth" : 25 * mm});
        }
        {
            var Q0;
            Q0=makeQuery(id+"F44.opExtrude","CAP_FACE",FACE,{"disambiguationData":[OSD([sQuery(id+"F43.wireOp",EDGE,"E107"),sQuery(id+"F43.wireOp",EDGE,"E108.0")])],"isStart":false});
            var sketch = newSketch(context, id + "F47", { "sketchPlane" : qUnion([Q0])});
            skCircle(sketch, "E118", {"center": v(7.38, 12.15) * mm, "radius": 6.25 * mm});
            skSolve(sketch);
        }
        {
            var Q0;
            Q0 = qSketchRegion(id + "F47", true);
            extrude(context, id + "F48", {"entities" : qUnion([Q0]), "operationType" : NewBodyOperationType.REMOVE, "oppositeDirection" : true, "depth" : .5 * mm});
        }
        {
            var Q0;
            Q0=makeQuery(id+"F44.opExtrude","CAP_FACE",FACE,{"disambiguationData":[OSD([sQuery(id+"F43.wireOp",EDGE,"E107"),sQuery(id+"F43.wireOp",EDGE,"E108.0")])],"isStart":false});
            var sketch = newSketch(context, id + "F49", { "sketchPlane" : qUnion([Q0])});
            skCircle(sketch, "E119", {"center": v(7.38, 12.15) * mm, "radius": 3.8 * mm});
            skSolve(sketch);
        }
        {
            var Q0;
            Q0 = qSketchRegion(id + "F49", true);
            extrude(context, id + "F50", {"entities" : qUnion([Q0]), "operationType" : NewBodyOperationType.REMOVE, "oppositeDirection" : true, "depth" : 4.2 * mm});
        }
        {
            var Q0;
            Q0=qCreatedBy(makeId("Front.planeOp"),FACE);
            var Q1;
            Q1=makeQuery(id+"F21.opExtrude","CAP_EDGE",EDGE,{"disambiguationData":[OSD([sQuery(id+"F20.wireOp",EDGE,"E42.top")])],"isStart":false});
            cPlane(context, id + "F51", {"entities" : qUnion([Q0, Q1]), "cplaneType" : CPlaneType.LINE_ANGLE, "offset" : 25 * mm, "angle" : 45 * degree, "oppositeDirection" : true, "width" : 150 * mm, "height" : 150 * mm});
        }
        {
            var Q0;
            Q0=makeQuery(id+"F1.opRevolve","SWEPT_BODY",BODY,{"disambiguationData":[OSD([sQuery(id+"F0.wireOp",EDGE,"E1"),sQuery(id+"F0.wireOp",EDGE,"E2"),sQuery(id+"F0.wireOp",EDGE,"E3"),sQuery(id+"F0.wireOp",EDGE,"E4"),sQuery(id+"F0.wireOp",EDGE,"E5"),sQuery(id+"F0.wireOp",EDGE,"E6"),sQuery(id+"F0.wireOp",EDGE,"E7"),sQuery(id+"F0.wireOp",EDGE,"E8"),sQuery(id+"F0.wireOp",EDGE,"E9"),sQuery(id+"F0.wireOp",EDGE,"E10"),sQuery(id+"F0.wireOp",EDGE,"E11")])]});
            var Q1;
            Q1=makeQuery(id+"F17.opExtrude","SWEPT_BODY",BODY,{"disambiguationData":[OSD([sQuery(id+"F0.wireOp",EDGE,"E6"),sQuery(id+"F0.wireOp",EDGE,"E7"),sQuery(id+"F16.wireOp",EDGE,"E40")])]});
            var Q2;
            Q2=makeQuery(id+"F25.opExtrude","SWEPT_BODY",BODY,{"disambiguationData":[OSD([sQuery(id+"F0.wireOp",EDGE,"E3"),sQuery(id+"F4.wireOp",EDGE,"E27.16.1"),sQuery(id+"F24.wireOp",EDGE,"E63"),sQuery(id+"F24.wireOp",EDGE,"E65"),sQuery(id+"F24.wireOp",EDGE,"E66.MirrorC"),sQuery(id+"F24.wireOp",EDGE,"E67"),sQuery(id+"F24.wireOp",EDGE,"E68.MirrorCS"),sQuery(id+"F24.wireOp",EDGE,"E69.1.0"),sQuery(id+"F24.wireOp",EDGE,"E69.1.1"),sQuery(id+"F24.wireOp",EDGE,"E69.1.2"),sQuery(id+"F24.wireOp",EDGE,"E69.1.3"),sQuery(id+"F24.wireOp",EDGE,"E69.1.4"),sQuery(id+"F24.wireOp",EDGE,"E69.2.0"),sQuery(id+"F24.wireOp",EDGE,"E69.2.1"),sQuery(id+"F24.wireOp",EDGE,"E69.2.2"),sQuery(id+"F24.wireOp",EDGE,"E69.2.3"),sQuery(id+"F24.wireOp",EDGE,"E69.2.4"),sQuery(id+"F24.wireOp",EDGE,"E69.3.0"),sQuery(id+"F24.wireOp",EDGE,"E69.3.1"),sQuery(id+"F24.wireOp",EDGE,"E69.3.2"),sQuery(id+"F24.wireOp",EDGE,"E69.3.3"),sQuery(id+"F24.wireOp",EDGE,"E69.3.4"),sQuery(id+"F24.wireOp",EDGE,"E69.4.0"),sQuery(id+"F24.wireOp",EDGE,"E69.4.1"),sQuery(id+"F24.wireOp",EDGE,"E69.4.2"),sQuery(id+"F24.wireOp",EDGE,"E69.4.3"),sQuery(id+"F24.wireOp",EDGE,"E69.4.4"),sQuery(id+"F24.wireOp",EDGE,"E69.5.0"),sQuery(id+"F24.wireOp",EDGE,"E69.5.1"),sQuery(id+"F24.wireOp",EDGE,"E69.5.2"),sQuery(id+"F24.wireOp",EDGE,"E69.5.3"),sQuery(id+"F24.wireOp",EDGE,"E69.5.4"),sQuery(id+"F24.wireOp",EDGE,"E69.6.0"),sQuery(id+"F24.wireOp",EDGE,"E69.6.1"),sQuery(id+"F24.wireOp",EDGE,"E69.6.2"),sQuery(id+"F24.wireOp",EDGE,"E69.6.3"),sQuery(id+"F24.wireOp",EDGE,"E69.6.4"),sQuery(id+"F24.wireOp",EDGE,"E69.7.0"),sQuery(id+"F24.wireOp",EDGE,"E69.7.1"),sQuery(id+"F24.wireOp",EDGE,"E69.7.2"),sQuery(id+"F24.wireOp",EDGE,"E69.7.3"),sQuery(id+"F24.wireOp",EDGE,"E69.7.4"),sQuery(id+"F24.wireOp",EDGE,"E69.8.0"),sQuery(id+"F24.wireOp",EDGE,"E69.8.1"),sQuery(id+"F24.wireOp",EDGE,"E69.8.2"),sQuery(id+"F24.wireOp",EDGE,"E69.8.3"),sQuery(id+"F24.wireOp",EDGE,"E69.8.4"),sQuery(id+"F24.wireOp",EDGE,"E69.9.0"),sQuery(id+"F24.wireOp",EDGE,"E69.9.1"),sQuery(id+"F24.wireOp",EDGE,"E69.9.2"),sQuery(id+"F24.wireOp",EDGE,"E69.9.3"),sQuery(id+"F24.wireOp",EDGE,"E69.9.4"),sQuery(id+"F24.wireOp",EDGE,"E69.10.0"),sQuery(id+"F24.wireOp",EDGE,"E69.10.1"),sQuery(id+"F24.wireOp",EDGE,"E69.10.2"),sQuery(id+"F24.wireOp",EDGE,"E69.10.3"),sQuery(id+"F24.wireOp",EDGE,"E69.10.4"),sQuery(id+"F24.wireOp",EDGE,"E70")])]});
            var Q3;
            Q3=makeQuery(id+"F40.opExtrude","SWEPT_BODY",BODY,{"disambiguationData":[OSD([sQuery(id+"F39.wireOp",EDGE,"E101"),sQuery(id+"F39.wireOp",EDGE,"E102"),sQuery(id+"F39.wireOp",EDGE,"E103.1.0"),sQuery(id+"F39.wireOp",EDGE,"E103.1.1"),sQuery(id+"F39.wireOp",EDGE,"E103.2.0"),sQuery(id+"F39.wireOp",EDGE,"E103.2.1"),sQuery(id+"F39.wireOp",EDGE,"E103.3.0"),sQuery(id+"F39.wireOp",EDGE,"E103.3.1"),sQuery(id+"F39.wireOp",EDGE,"E103.4.0"),sQuery(id+"F39.wireOp",EDGE,"E103.4.1"),sQuery(id+"F39.wireOp",EDGE,"E103.5.0"),sQuery(id+"F39.wireOp",EDGE,"E103.5.1"),sQuery(id+"F39.wireOp",EDGE,"E103.6.0"),sQuery(id+"F39.wireOp",EDGE,"E103.6.1"),sQuery(id+"F39.wireOp",EDGE,"E103.7.0"),sQuery(id+"F39.wireOp",EDGE,"E103.7.1"),sQuery(id+"F39.wireOp",EDGE,"E103.8.0"),sQuery(id+"F39.wireOp",EDGE,"E103.8.1"),sQuery(id+"F39.wireOp",EDGE,"E103.9.0"),sQuery(id+"F39.wireOp",EDGE,"E103.9.1"),sQuery(id+"F39.wireOp",EDGE,"E104")])]});
            var Q4;
            Q4=makeQuery(id+"F21.opExtrude","SWEPT_BODY",BODY,{"disambiguationData":[OSD([sQuery(id+"F20.wireOp",EDGE,"E42.bottom"),sQuery(id+"F20.wireOp",EDGE,"E42.top"),sQuery(id+"F20.wireOp",EDGE,"E42.left"),sQuery(id+"F20.wireOp",EDGE,"E42.right"),sQuery(id+"F20.wireOp",EDGE,"E52.0")])]});
            var Q5;
            Q5=qCreatedBy(id+"F51.planeOp",FACE);
            mirror(context, id + "F52", {"operationType" : NewBodyOperationType.ADD, "entities" : qUnion([Q0, Q1, Q2, Q3, Q4]), "mirrorPlane" : qUnion([Q5])});
        }
    });
